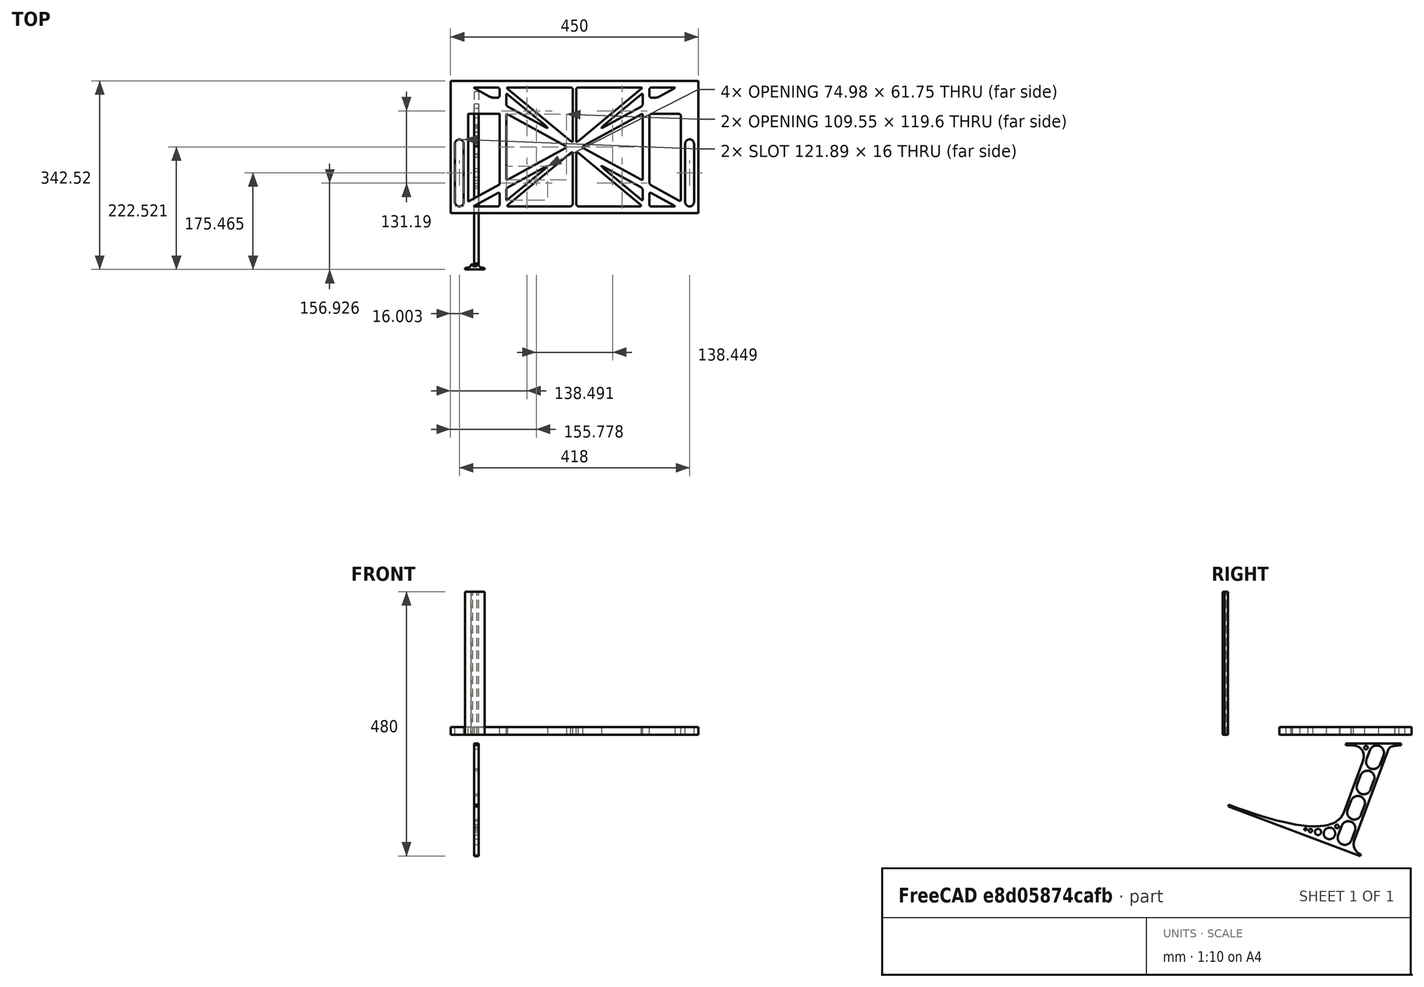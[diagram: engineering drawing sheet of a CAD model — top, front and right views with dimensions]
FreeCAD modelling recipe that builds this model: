
FCSTD DOCUMENT  (FreeCAD 0.19R0.19.2)
Label: laptopStand145FCStd
License: All rights reserved
LicenseURL: http://en.wikipedia.org/wiki/All_rights_reserved
objects: Sketcher::SketchObject×4, Part::Extrusion×3
note: 7 computed .brp shape members not serialized (recipe doc carries the construction recipe); baked Part::Feature solids carry a one-line shape summary decoded from their .brp

FEATURE [Sketcher::SketchObject] Sketch
  FullyConstrained = false
  sketch-geometry (349):
    g0: LineSegment StartX=-10.9272 StartY=-82.7794 StartZ=0 EndX=46.0728 EndY=-51.4823 EndZ=0
    g1: LineSegment StartX=-10.9272 StartY=76.4095 StartZ=0 EndX=-10.9272 EndY=-82.7794 EndZ=0
    g2: LineSegment StartX=46.0728 StartY=76.4095 StartZ=0 EndX=46.0728 EndY=-51.4823 EndZ=0
    g3: LineSegment StartX=-42.9272 StartY=136.221 StartZ=0 EndX=-42.9272 EndY=-103.779 EndZ=0
    g4: LineSegment StartX=407.073 StartY=136.221 StartZ=0 EndX=407.073 EndY=-103.779 EndZ=0
    g5: ArcOfCircle CenterX=-26.9272 CenterY=-83.7794 CenterZ=0 NormalX=0 NormalY=0 NormalZ=1 AngleXU=0 Radius=8 StartAngle=3.14159 EndAngle=6.28319
    g6: ArcOfCircle CenterX=391.073 CenterY=22.1087 CenterZ=0 NormalX=0 NormalY=0 NormalZ=1 AngleXU=0 Radius=8 StartAngle=-4.4e-15 EndAngle=3.14159
    g7: LineSegment StartX=399.073 StartY=22.1087 StartZ=0 EndX=399.073 EndY=-83.7794 EndZ=0
    g8: LineSegment StartX=383.073 StartY=22.1087 StartZ=0 EndX=383.073 EndY=-83.7794 EndZ=0
    g9: ArcOfCircle CenterX=391.073 CenterY=-83.7794 CenterZ=0 NormalX=0 NormalY=0 NormalZ=1 AngleXU=0 Radius=8 StartAngle=3.14159 EndAngle=6.28319
    g10: Circle CenterX=175.022 CenterY=27.0628 CenterZ=0 NormalX=0 NormalY=0 NormalZ=1 AngleXU=0 Radius=1
    g11: Circle CenterX=179.022 CenterY=24.8665 CenterZ=0 NormalX=0 NormalY=0 NormalZ=1 AngleXU=0 Radius=1
    g12: Circle CenterX=179.022 CenterY=27.0628 CenterZ=0 NormalX=0 NormalY=0 NormalZ=1 AngleXU=0 Radius=1
    g13: BSplineCurve PolesCount=3 KnotsCount=2 Degree=2 IsPeriodic=0
    g14: GeomPoint X=175.022 Y=27.0628 Z=0
    g15: GeomPoint X=179.022 Y=27.0628 Z=0
    g16: Circle CenterX=189.124 CenterY=27.0628 CenterZ=0 NormalX=0 NormalY=0 NormalZ=1 AngleXU=0 Radius=1
    g17: Circle CenterX=185.124 CenterY=24.8665 CenterZ=0 NormalX=0 NormalY=0 NormalZ=1 AngleXU=0 Radius=1
    g18: Circle CenterX=185.124 CenterY=27.0628 CenterZ=0 NormalX=0 NormalY=0 NormalZ=1 AngleXU=0 Radius=1
    g19: BSplineCurve PolesCount=3 KnotsCount=2 Degree=2 IsPeriodic=0
    g20: GeomPoint X=189.124 Y=27.0628 Z=0
    g21: GeomPoint X=185.124 Y=27.0628 Z=0
    g22: Circle CenterX=175.022 CenterY=5.37834 CenterZ=0 NormalX=0 NormalY=0 NormalZ=1 AngleXU=0 Radius=1
    g23: Circle CenterX=179.022 CenterY=7.57463 CenterZ=0 NormalX=0 NormalY=0 NormalZ=1 AngleXU=0 Radius=1
    g24: Circle CenterX=179.022 CenterY=5.34704 CenterZ=0 NormalX=0 NormalY=0 NormalZ=1 AngleXU=0 Radius=1
    g25: BSplineCurve PolesCount=3 KnotsCount=2 Degree=2 IsPeriodic=0
    g26: GeomPoint X=175.022 Y=5.37834 Z=0
    g27: GeomPoint X=179.022 Y=5.34704 Z=0
    g28: Circle CenterX=189.124 CenterY=5.37834 CenterZ=0 NormalX=0 NormalY=0 NormalZ=1 AngleXU=0 Radius=1
    g29: Circle CenterX=185.124 CenterY=7.57463 CenterZ=0 NormalX=0 NormalY=0 NormalZ=1 AngleXU=0 Radius=1
    g30: Circle CenterX=185.124 CenterY=5.34704 CenterZ=0 NormalX=0 NormalY=0 NormalZ=1 AngleXU=0 Radius=1
    g31: BSplineCurve PolesCount=3 KnotsCount=2 Degree=2 IsPeriodic=0
    g32: GeomPoint X=189.124 Y=5.37834 Z=0
    g33: GeomPoint X=185.124 Y=5.34704 Z=0
    g34: Circle CenterX=165.871 CenterY=18.1458 CenterZ=0 NormalX=0 NormalY=0 NormalZ=1 AngleXU=0 Radius=1
    g35: Circle CenterX=169.377 CenterY=16.2206 CenterZ=0 NormalX=0 NormalY=0 NormalZ=1 AngleXU=0 Radius=1
    g36: Circle CenterX=165.871 CenterY=14.2954 CenterZ=0 NormalX=0 NormalY=0 NormalZ=1 AngleXU=0 Radius=1
    g37: BSplineCurve PolesCount=3 KnotsCount=2 Degree=2 IsPeriodic=0
    g38: GeomPoint X=165.871 Y=18.1458 Z=0
    g39: GeomPoint X=165.871 Y=14.2954 Z=0
    g40: Circle CenterX=198.275 CenterY=18.1458 CenterZ=0 NormalX=0 NormalY=0 NormalZ=1 AngleXU=0 Radius=1
    g41: Circle CenterX=194.768 CenterY=16.2206 CenterZ=0 NormalX=0 NormalY=0 NormalZ=1 AngleXU=0 Radius=1
    g42: Circle CenterX=198.275 CenterY=14.2954 CenterZ=0 NormalX=0 NormalY=0 NormalZ=1 AngleXU=0 Radius=1
    g43: BSplineCurve PolesCount=3 KnotsCount=2 Degree=2 IsPeriodic=0
    g44: GeomPoint X=198.275 Y=18.1458 Z=0
    g45: GeomPoint X=198.275 Y=14.2954 Z=0
    g46: LineSegment StartX=407.073 StartY=-103.779 StartZ=0 EndX=-42.9272 EndY=-103.779 EndZ=0
    g47: LineSegment StartX=407.073 StartY=136.221 StartZ=0 EndX=-42.9272 EndY=136.221 EndZ=0
    g48: LineSegment StartX=46.0728 StartY=76.4095 StartZ=0 EndX=-10.9272 EndY=76.4095 EndZ=0
    g49: Circle CenterX=125.607 CenterY=54.1951 CenterZ=0 NormalX=0 NormalY=0 NormalZ=1 AngleXU=0 Radius=1
    g50: Circle CenterX=139.632 CenterY=46.4944 CenterZ=0 NormalX=0 NormalY=0 NormalZ=1 AngleXU=0 Radius=1
    g51: Circle CenterX=127.326 CenterY=56.7187 CenterZ=0 NormalX=0 NormalY=0 NormalZ=1 AngleXU=0 Radius=1
    g52: BSplineCurve PolesCount=3 KnotsCount=2 Degree=2 IsPeriodic=0
    g53: GeomPoint X=125.607 Y=54.1951 Z=0
    g54: GeomPoint X=127.326 Y=56.7187 Z=0
    g55: Circle CenterX=236.821 CenterY=56.7187 CenterZ=0 NormalX=0 NormalY=0 NormalZ=1 AngleXU=0 Radius=1
    g56: Circle CenterX=224.513 CenterY=46.4944 CenterZ=0 NormalX=0 NormalY=0 NormalZ=1 AngleXU=0 Radius=1
    g57: Circle CenterX=238.538 CenterY=54.1951 CenterZ=0 NormalX=0 NormalY=0 NormalZ=1 AngleXU=0 Radius=1
    g58: BSplineCurve PolesCount=3 KnotsCount=2 Degree=2 IsPeriodic=0
    g59: GeomPoint X=236.821 Y=56.7187 Z=0
    g60: GeomPoint X=238.538 Y=54.1951 Z=0
    g61: Circle CenterX=238.538 CenterY=-21.7539 CenterZ=0 NormalX=0 NormalY=0 NormalZ=1 AngleXU=0 Radius=1
    g62: Circle CenterX=224.513 CenterY=-14.0532 CenterZ=0 NormalX=0 NormalY=0 NormalZ=1 AngleXU=0 Radius=1
    g63: Circle CenterX=236.821 CenterY=-24.2775 CenterZ=0 NormalX=0 NormalY=0 NormalZ=1 AngleXU=0 Radius=1
    g64: BSplineCurve PolesCount=3 KnotsCount=2 Degree=2 IsPeriodic=0
    g65: GeomPoint X=238.538 Y=-21.7539 Z=0
    g66: GeomPoint X=236.821 Y=-24.2775 Z=0
    g67: Circle CenterX=125.607 CenterY=-21.7539 CenterZ=0 NormalX=0 NormalY=0 NormalZ=1 AngleXU=0 Radius=1
    g68: Circle CenterX=139.632 CenterY=-14.0532 CenterZ=0 NormalX=0 NormalY=0 NormalZ=1 AngleXU=0 Radius=1
    g69: Circle CenterX=127.325 CenterY=-24.2775 CenterZ=0 NormalX=0 NormalY=0 NormalZ=1 AngleXU=0 Radius=1
    g70: BSplineCurve PolesCount=3 KnotsCount=2 Degree=2 IsPeriodic=0
    g71: GeomPoint X=125.607 Y=-21.7539 Z=0
    g72: GeomPoint X=127.325 Y=-24.2775 Z=0
    g73: Circle CenterX=302.996 CenterY=111.695 CenterZ=0 NormalX=0 NormalY=0 NormalZ=1 AngleXU=0 Radius=1
    g74: Circle CenterX=306.073 CenterY=114.251 CenterZ=0 NormalX=0 NormalY=0 NormalZ=1 AngleXU=0 Radius=1
    g75: Circle CenterX=306.073 CenterY=110.251 CenterZ=0 NormalX=0 NormalY=0 NormalZ=1 AngleXU=0 Radius=1
    g76: BSplineCurve PolesCount=3 KnotsCount=2 Degree=2 IsPeriodic=0
    g77: GeomPoint X=302.996 Y=111.695 Z=0
    g78: GeomPoint X=306.073 Y=110.251 Z=0
    g79: Circle CenterX=306.073 CenterY=95.2763 CenterZ=0 NormalX=0 NormalY=0 NormalZ=1 AngleXU=0 Radius=1
    g80: Circle CenterX=306.073 CenterY=91.2763 CenterZ=0 NormalX=0 NormalY=0 NormalZ=1 AngleXU=0 Radius=1
    g81: Circle CenterX=302.567 CenterY=89.3511 CenterZ=0 NormalX=0 NormalY=0 NormalZ=1 AngleXU=0 Radius=1
    g82: BSplineCurve PolesCount=3 KnotsCount=2 Degree=2 IsPeriodic=0
    g83: GeomPoint X=306.073 Y=95.2763 Z=0
    g84: GeomPoint X=302.567 Y=89.3511 Z=0
    g85: LineSegment StartX=306.073 StartY=110.251 StartZ=0 EndX=306.073 EndY=95.2763 EndZ=0
    g86: LineSegment StartX=302.996 StartY=111.695 StartZ=0 EndX=236.821 EndY=56.7187 EndZ=0
    g87: LineSegment StartX=238.538 StartY=54.1951 StartZ=0 EndX=302.567 EndY=89.3511 EndZ=0
    g88: Circle CenterX=61.1496 CenterY=111.695 CenterZ=0 NormalX=0 NormalY=0 NormalZ=1 AngleXU=0 Radius=1
    g89: Circle CenterX=58.0728 CenterY=114.251 CenterZ=0 NormalX=0 NormalY=0 NormalZ=1 AngleXU=0 Radius=1
    g90: Circle CenterX=58.0728 CenterY=110.251 CenterZ=0 NormalX=0 NormalY=0 NormalZ=1 AngleXU=0 Radius=1
    g91: BSplineCurve PolesCount=3 KnotsCount=2 Degree=2 IsPeriodic=0
    g92: GeomPoint X=61.1496 Y=111.695 Z=0
    g93: GeomPoint X=58.0728 Y=110.251 Z=0
    g94: Circle CenterX=61.5791 CenterY=89.3511 CenterZ=0 NormalX=0 NormalY=0 NormalZ=1 AngleXU=0 Radius=1
    g95: Circle CenterX=58.0728 CenterY=91.2763 CenterZ=0 NormalX=0 NormalY=0 NormalZ=1 AngleXU=0 Radius=1
    g96: Circle CenterX=58.0728 CenterY=95.2763 CenterZ=0 NormalX=0 NormalY=0 NormalZ=1 AngleXU=0 Radius=1
    g97: BSplineCurve PolesCount=3 KnotsCount=2 Degree=2 IsPeriodic=0
    g98: GeomPoint X=61.5791 Y=89.3511 Z=0
    g99: GeomPoint X=58.0728 Y=95.2763 Z=0
    g100: LineSegment StartX=58.0728 StartY=110.251 StartZ=0 EndX=58.0728 EndY=95.2763 EndZ=0
    g101: LineSegment StartX=61.1496 StartY=111.695 StartZ=0 EndX=127.326 EndY=56.7187 EndZ=0
    g102: LineSegment StartX=125.607 StartY=54.1951 StartZ=0 EndX=61.5791 EndY=89.3511 EndZ=0
    g103: Circle CenterX=61.5791 CenterY=-56.9099 CenterZ=0 NormalX=0 NormalY=0 NormalZ=1 AngleXU=0 Radius=1
    g104: Circle CenterX=58.0728 CenterY=-58.8351 CenterZ=0 NormalX=0 NormalY=0 NormalZ=1 AngleXU=0 Radius=1
    g105: Circle CenterX=58.0728 CenterY=-62.8351 CenterZ=0 NormalX=0 NormalY=0 NormalZ=1 AngleXU=0 Radius=1
    g106: BSplineCurve PolesCount=3 KnotsCount=2 Degree=2 IsPeriodic=0
    g107: GeomPoint X=61.5791 Y=-56.9099 Z=0
    g108: GeomPoint X=58.0728 Y=-62.8351 Z=0
    g109: Circle CenterX=58.0728 CenterY=-77.8102 CenterZ=0 NormalX=0 NormalY=0 NormalZ=1 AngleXU=0 Radius=1
    g110: Circle CenterX=58.0728 CenterY=-81.8102 CenterZ=0 NormalX=0 NormalY=0 NormalZ=1 AngleXU=0 Radius=1
    g111: Circle CenterX=61.1496 CenterY=-79.2541 CenterZ=0 NormalX=0 NormalY=0 NormalZ=1 AngleXU=0 Radius=1
    g112: BSplineCurve PolesCount=3 KnotsCount=2 Degree=2 IsPeriodic=0
    g113: GeomPoint X=58.0728 Y=-77.8102 Z=0
    g114: GeomPoint X=61.1496 Y=-79.2541 Z=0
    g115: LineSegment StartX=58.0728 StartY=-62.8351 StartZ=0 EndX=58.0728 EndY=-77.8102 EndZ=0
    g116: LineSegment StartX=61.1496 StartY=-79.2541 StartZ=0 EndX=127.325 EndY=-24.2775 EndZ=0
    g117: LineSegment StartX=125.607 StartY=-21.7539 StartZ=0 EndX=61.5791 EndY=-56.9099 EndZ=0
    g118: Circle CenterX=302.567 CenterY=-56.9099 CenterZ=0 NormalX=0 NormalY=0 NormalZ=1 AngleXU=0 Radius=1
    g119: Circle CenterX=306.073 CenterY=-58.8351 CenterZ=0 NormalX=0 NormalY=0 NormalZ=1 AngleXU=0 Radius=1
    g120: Circle CenterX=306.073 CenterY=-62.8351 CenterZ=0 NormalX=0 NormalY=0 NormalZ=1 AngleXU=0 Radius=1
    g121: BSplineCurve PolesCount=3 KnotsCount=2 Degree=2 IsPeriodic=0
    g122: GeomPoint X=302.567 Y=-56.9099 Z=0
    g123: GeomPoint X=306.073 Y=-62.8351 Z=0
    g124: Circle CenterX=302.996 CenterY=-79.2541 CenterZ=0 NormalX=0 NormalY=0 NormalZ=1 AngleXU=0 Radius=1
    g125: Circle CenterX=306.073 CenterY=-81.8102 CenterZ=0 NormalX=0 NormalY=0 NormalZ=1 AngleXU=0 Radius=1
    g126: Circle CenterX=306.073 CenterY=-77.8102 CenterZ=0 NormalX=0 NormalY=0 NormalZ=1 AngleXU=0 Radius=1
    g127: BSplineCurve PolesCount=3 KnotsCount=2 Degree=2 IsPeriodic=0
    g128: GeomPoint X=302.996 Y=-79.2541 Z=0
    g129: GeomPoint X=306.073 Y=-77.8102 Z=0
    g130: LineSegment StartX=306.073 StartY=-62.8351 StartZ=0 EndX=306.073 EndY=-77.8102 EndZ=0
    g131: LineSegment StartX=302.996 StartY=-79.2541 StartZ=0 EndX=236.821 EndY=-24.2775 EndZ=0
    g132: LineSegment StartX=238.538 StartY=-21.7539 StartZ=0 EndX=302.567 EndY=-56.9099 EndZ=0
    g133: Circle CenterX=61.6457 CenterY=-88.8112 CenterZ=0 NormalX=0 NormalY=0 NormalZ=1 AngleXU=0 Radius=1
    g134: Circle CenterX=58.0728 CenterY=-91.7794 CenterZ=0 NormalX=0 NormalY=0 NormalZ=1 AngleXU=0 Radius=1
    g135: Circle CenterX=63.9135 CenterY=-91.7794 CenterZ=0 NormalX=0 NormalY=0 NormalZ=1 AngleXU=0 Radius=1
    g136: BSplineCurve PolesCount=3 KnotsCount=2 Degree=2 IsPeriodic=0
    g137: GeomPoint X=61.6457 Y=-88.8112 Z=0
    g138: GeomPoint X=63.9135 Y=-91.7794 Z=0
    g139: Circle CenterX=179.022 CenterY=-85.8163 CenterZ=0 NormalX=0 NormalY=0 NormalZ=1 AngleXU=0 Radius=1
    g140: Circle CenterX=179.022 CenterY=-91.7794 CenterZ=0 NormalX=0 NormalY=0 NormalZ=1 AngleXU=0 Radius=1
    g141: Circle CenterX=171.895 CenterY=-91.7794 CenterZ=0 NormalX=0 NormalY=0 NormalZ=1 AngleXU=0 Radius=1
    g142: BSplineCurve PolesCount=3 KnotsCount=2 Degree=2 IsPeriodic=0
    g143: GeomPoint X=179.022 Y=-85.8163 Z=0
    g144: GeomPoint X=171.895 Y=-91.7794 Z=0
    g145: Circle CenterX=185.124 CenterY=-86.2028 CenterZ=0 NormalX=0 NormalY=0 NormalZ=1 AngleXU=0 Radius=1
    g146: Circle CenterX=185.124 CenterY=-91.7794 CenterZ=0 NormalX=0 NormalY=0 NormalZ=1 AngleXU=0 Radius=1
    g147: Circle CenterX=191.747 CenterY=-91.7794 CenterZ=0 NormalX=0 NormalY=0 NormalZ=1 AngleXU=0 Radius=1
    g148: BSplineCurve PolesCount=3 KnotsCount=2 Degree=2 IsPeriodic=0
    g149: GeomPoint X=185.124 Y=-86.2028 Z=0
    g150: GeomPoint X=191.747 Y=-91.7794 Z=0
    g151: Circle CenterX=299.888 CenterY=-86.6413 CenterZ=0 NormalX=0 NormalY=0 NormalZ=1 AngleXU=0 Radius=1
    g152: Circle CenterX=306.073 CenterY=-91.7794 CenterZ=0 NormalX=0 NormalY=0 NormalZ=1 AngleXU=0 Radius=1
    g153: Circle CenterX=298.776 CenterY=-91.7794 CenterZ=0 NormalX=0 NormalY=0 NormalZ=1 AngleXU=0 Radius=1
    g154: BSplineCurve PolesCount=3 KnotsCount=2 Degree=2 IsPeriodic=0
    g155: GeomPoint X=299.888 Y=-86.6413 Z=0
    g156: GeomPoint X=298.776 Y=-91.7794 Z=0
    g157: LineSegment StartX=189.124 StartY=5.37834 StartZ=0 EndX=299.888 EndY=-86.6413 EndZ=0
    g158: LineSegment StartX=298.776 StartY=-91.7794 StartZ=0 EndX=191.747 EndY=-91.7794 EndZ=0
    g159: LineSegment StartX=185.124 StartY=-86.2028 StartZ=0 EndX=185.124 EndY=5.34704 EndZ=0
    g160: LineSegment StartX=179.022 StartY=5.34704 StartZ=0 EndX=179.022 EndY=-85.8163 EndZ=0
    g161: LineSegment StartX=171.895 StartY=-91.7794 StartZ=0 EndX=63.9135 EndY=-91.7794 EndZ=0
    g162: LineSegment StartX=61.6457 StartY=-88.8112 StartZ=0 EndX=175.022 EndY=5.37834 EndZ=0
    g163: Circle CenterX=302.073 CenterY=124.221 CenterZ=0 NormalX=0 NormalY=0 NormalZ=1 AngleXU=0 Radius=1
    g164: Circle CenterX=306.073 CenterY=124.221 CenterZ=0 NormalX=0 NormalY=0 NormalZ=1 AngleXU=0 Radius=1
    g165: Circle CenterX=302.996 CenterY=121.665 CenterZ=0 NormalX=0 NormalY=0 NormalZ=1 AngleXU=0 Radius=1
    g166: BSplineCurve PolesCount=3 KnotsCount=2 Degree=2 IsPeriodic=0
    g167: GeomPoint X=302.073 Y=124.221 Z=0
    g168: GeomPoint X=302.996 Y=121.665 Z=0
    g169: Circle CenterX=189.124 CenterY=124.221 CenterZ=0 NormalX=0 NormalY=0 NormalZ=1 AngleXU=0 Radius=1
    g170: Circle CenterX=185.124 CenterY=124.221 CenterZ=0 NormalX=0 NormalY=0 NormalZ=1 AngleXU=0 Radius=1
    g171: Circle CenterX=185.124 CenterY=120.221 CenterZ=0 NormalX=0 NormalY=0 NormalZ=1 AngleXU=0 Radius=1
    g172: BSplineCurve PolesCount=3 KnotsCount=2 Degree=2 IsPeriodic=0
    g173: GeomPoint X=189.124 Y=124.221 Z=0
    g174: GeomPoint X=185.124 Y=120.221 Z=0
    g175: Circle CenterX=175.022 CenterY=124.221 CenterZ=0 NormalX=0 NormalY=0 NormalZ=1 AngleXU=0 Radius=1
    g176: Circle CenterX=179.022 CenterY=124.221 CenterZ=0 NormalX=0 NormalY=0 NormalZ=1 AngleXU=0 Radius=1
    g177: Circle CenterX=179.022 CenterY=120.221 CenterZ=0 NormalX=0 NormalY=0 NormalZ=1 AngleXU=0 Radius=1
    g178: BSplineCurve PolesCount=3 KnotsCount=2 Degree=2 IsPeriodic=0
    g179: GeomPoint X=175.022 Y=124.221 Z=0
    g180: GeomPoint X=179.022 Y=120.221 Z=0
    g181: Circle CenterX=62.0728 CenterY=124.221 CenterZ=0 NormalX=0 NormalY=0 NormalZ=1 AngleXU=0 Radius=1
    g182: Circle CenterX=58.0728 CenterY=124.221 CenterZ=0 NormalX=0 NormalY=0 NormalZ=1 AngleXU=0 Radius=1
    g183: Circle CenterX=61.1496 CenterY=121.665 CenterZ=0 NormalX=0 NormalY=0 NormalZ=1 AngleXU=0 Radius=1
    g184: BSplineCurve PolesCount=3 KnotsCount=2 Degree=2 IsPeriodic=0
    g185: GeomPoint X=62.0728 Y=124.221 Z=0
    g186: GeomPoint X=61.1496 Y=121.665 Z=0
    g187: LineSegment StartX=62.0728 StartY=124.221 StartZ=0 EndX=175.022 EndY=124.221 EndZ=0
    g188: LineSegment StartX=179.022 StartY=120.221 StartZ=0 EndX=179.022 EndY=27.0628 EndZ=0
    g189: LineSegment StartX=185.124 StartY=27.0628 StartZ=0 EndX=185.124 EndY=120.221 EndZ=0
    g190: LineSegment StartX=189.124 StartY=124.221 StartZ=0 EndX=302.073 EndY=124.221 EndZ=0
    g191: LineSegment StartX=302.996 StartY=121.665 StartZ=0 EndX=189.124 EndY=27.0628 EndZ=0
    g192: LineSegment StartX=175.022 StartY=27.0628 StartZ=0 EndX=61.1496 EndY=121.665 EndZ=0
    g193: Circle CenterX=61.5791 CenterY=75.4095 CenterZ=0 NormalX=0 NormalY=0 NormalZ=1 AngleXU=0 Radius=1
    g194: Circle CenterX=58.0728 CenterY=77.3346 CenterZ=0 NormalX=0 NormalY=0 NormalZ=1 AngleXU=0 Radius=1
    g195: Circle CenterX=58.0728 CenterY=73.3346 CenterZ=0 NormalX=0 NormalY=0 NormalZ=1 AngleXU=0 Radius=1
    g196: BSplineCurve PolesCount=3 KnotsCount=2 Degree=2 IsPeriodic=0
    g197: GeomPoint X=61.5791 Y=75.4095 Z=0
    g198: GeomPoint X=58.0728 Y=73.3346 Z=0
    g199: Circle CenterX=58.0728 CenterY=-40.8935 CenterZ=0 NormalX=0 NormalY=0 NormalZ=1 AngleXU=0 Radius=1
    g200: Circle CenterX=58.0728 CenterY=-44.8935 CenterZ=0 NormalX=0 NormalY=0 NormalZ=1 AngleXU=0 Radius=1
    g201: Circle CenterX=61.5791 CenterY=-42.9683 CenterZ=0 NormalX=0 NormalY=0 NormalZ=1 AngleXU=0 Radius=1
    g202: BSplineCurve PolesCount=3 KnotsCount=2 Degree=2 IsPeriodic=0
    g203: GeomPoint X=58.0728 Y=-40.8935 Z=0
    g204: GeomPoint X=61.5791 Y=-42.9683 Z=0
    g205: LineSegment StartX=61.5791 StartY=-42.9683 StartZ=0 EndX=165.871 EndY=14.2954 EndZ=0
    g206: LineSegment StartX=165.871 StartY=18.1458 StartZ=0 EndX=61.5791 EndY=75.4095 EndZ=0
    g207: LineSegment StartX=58.0728 StartY=73.3346 StartZ=0 EndX=58.0728 EndY=-40.8935 EndZ=0
    g208: Circle CenterX=302.567 CenterY=-42.9683 CenterZ=0 NormalX=0 NormalY=0 NormalZ=1 AngleXU=0 Radius=1
    g209: Circle CenterX=306.073 CenterY=-44.8935 CenterZ=0 NormalX=0 NormalY=0 NormalZ=1 AngleXU=0 Radius=1
    g210: Circle CenterX=306.073 CenterY=-40.8935 CenterZ=0 NormalX=0 NormalY=0 NormalZ=1 AngleXU=0 Radius=1
    g211: BSplineCurve PolesCount=3 KnotsCount=2 Degree=2 IsPeriodic=0
    g212: GeomPoint X=302.567 Y=-42.9683 Z=0
    g213: GeomPoint X=306.073 Y=-40.8935 Z=0
    g214: Circle CenterX=306.073 CenterY=73.3346 CenterZ=0 NormalX=0 NormalY=0 NormalZ=1 AngleXU=0 Radius=1
    g215: Circle CenterX=306.073 CenterY=77.3346 CenterZ=0 NormalX=0 NormalY=0 NormalZ=1 AngleXU=0 Radius=1
    g216: Circle CenterX=302.567 CenterY=75.4095 CenterZ=0 NormalX=0 NormalY=0 NormalZ=1 AngleXU=0 Radius=1
    g217: BSplineCurve PolesCount=3 KnotsCount=2 Degree=2 IsPeriodic=0
    g218: GeomPoint X=306.073 Y=73.3346 Z=0
    g219: GeomPoint X=302.567 Y=75.4095 Z=0
    g220: LineSegment StartX=302.567 StartY=-42.9683 StartZ=0 EndX=198.275 EndY=14.2954 EndZ=0
    g221: LineSegment StartX=198.275 StartY=18.1458 StartZ=0 EndX=302.567 EndY=75.4095 EndZ=0
    g222: LineSegment StartX=306.073 StartY=73.3346 StartZ=0 EndX=306.073 EndY=-40.8935 EndZ=0
    g223: LineSegment StartX=322.073 StartY=105.865 StartZ=0 EndX=328.643 EndY=105.865 EndZ=0
    g224: LineSegment StartX=318.073 StartY=120.221 StartZ=0 EndX=318.073 EndY=109.865 EndZ=0
    g225: LineSegment StartX=336.157 StartY=107.779 StartZ=0 EndX=362.567 EndY=122.294 EndZ=0
    g226: Circle CenterX=362.073 CenterY=124.221 CenterZ=0 NormalX=0 NormalY=0 NormalZ=1 AngleXU=0 Radius=1
    g227: Circle CenterX=366.073 CenterY=124.221 CenterZ=0 NormalX=0 NormalY=0 NormalZ=1 AngleXU=0 Radius=1
    g228: Circle CenterX=362.567 CenterY=122.294 CenterZ=0 NormalX=0 NormalY=0 NormalZ=1 AngleXU=0 Radius=1
    g229: BSplineCurve PolesCount=3 KnotsCount=2 Degree=2 IsPeriodic=0
    g230: GeomPoint X=362.073 Y=124.221 Z=0
    g231: GeomPoint X=362.567 Y=122.294 Z=0
    g232: Circle CenterX=322.073 CenterY=124.221 CenterZ=0 NormalX=0 NormalY=0 NormalZ=1 AngleXU=0 Radius=1
    g233: Circle CenterX=318.073 CenterY=124.221 CenterZ=0 NormalX=0 NormalY=0 NormalZ=1 AngleXU=0 Radius=1
    g234: Circle CenterX=318.073 CenterY=120.221 CenterZ=0 NormalX=0 NormalY=0 NormalZ=1 AngleXU=0 Radius=1
    g235: BSplineCurve PolesCount=3 KnotsCount=2 Degree=2 IsPeriodic=0
    g236: GeomPoint X=322.073 Y=124.221 Z=0
    g237: GeomPoint X=318.073 Y=120.221 Z=0
    g238: Circle CenterX=322.073 CenterY=105.865 CenterZ=0 NormalX=0 NormalY=0 NormalZ=1 AngleXU=0 Radius=1
    g239: Circle CenterX=318.073 CenterY=105.865 CenterZ=0 NormalX=0 NormalY=0 NormalZ=1 AngleXU=0 Radius=1
    g240: Circle CenterX=318.073 CenterY=109.865 CenterZ=0 NormalX=0 NormalY=0 NormalZ=1 AngleXU=0 Radius=1
    g241: BSplineCurve PolesCount=3 KnotsCount=2 Degree=2 IsPeriodic=0
    g242: GeomPoint X=322.073 Y=105.865 Z=0
    g243: GeomPoint X=318.073 Y=109.865 Z=0
    g244: Circle CenterX=336.157 CenterY=107.779 CenterZ=0 NormalX=0 NormalY=0 NormalZ=1 AngleXU=0 Radius=1
    g245: Circle CenterX=332.651 CenterY=105.853 CenterZ=0 NormalX=0 NormalY=0 NormalZ=1 AngleXU=0 Radius=1
    g246: Circle CenterX=328.643 CenterY=105.865 CenterZ=0 NormalX=0 NormalY=0 NormalZ=1 AngleXU=0 Radius=1
    g247: BSplineCurve PolesCount=3 KnotsCount=2 Degree=2 IsPeriodic=0
    g248: GeomPoint X=336.157 Y=107.779 Z=0
    g249: GeomPoint X=328.643 Y=105.865 Z=0
    g250: LineSegment StartX=322.073 StartY=124.221 StartZ=0 EndX=362.073 EndY=124.221 EndZ=0
    g251: Circle CenterX=371.567 CenterY=-80.8644 CenterZ=0 NormalX=0 NormalY=0 NormalZ=1 AngleXU=0 Radius=1
    g252: Circle CenterX=375.073 CenterY=-82.7896 CenterZ=0 NormalX=0 NormalY=0 NormalZ=1 AngleXU=0 Radius=1
    g253: Circle CenterX=375.073 CenterY=-78.7896 CenterZ=0 NormalX=0 NormalY=0 NormalZ=1 AngleXU=0 Radius=1
    g254: BSplineCurve PolesCount=3 KnotsCount=2 Degree=2 IsPeriodic=0
    g255: GeomPoint X=371.567 Y=-80.8644 Z=0
    g256: GeomPoint X=375.073 Y=-78.7896 Z=0
    g257: Circle CenterX=321.579 CenterY=-53.4075 CenterZ=0 NormalX=0 NormalY=0 NormalZ=1 AngleXU=0 Radius=1
    g258: Circle CenterX=318.073 CenterY=-51.4823 CenterZ=0 NormalX=0 NormalY=0 NormalZ=1 AngleXU=0 Radius=1
    g259: Circle CenterX=318.073 CenterY=-47.4805 CenterZ=0 NormalX=0 NormalY=0 NormalZ=1 AngleXU=0 Radius=1
    g260: BSplineCurve PolesCount=3 KnotsCount=2 Degree=2 IsPeriodic=0
    g261: GeomPoint X=321.579 Y=-53.4075 Z=0
    g262: GeomPoint X=318.073 Y=-47.4805 Z=0
    g263: LineSegment StartX=371.567 StartY=-80.8644 StartZ=0 EndX=321.579 EndY=-53.4075 EndZ=0
    g264: Circle CenterX=321.579 CenterY=-67.3492 CenterZ=0 NormalX=0 NormalY=0 NormalZ=1 AngleXU=0 Radius=1
    g265: Circle CenterX=318.073 CenterY=-65.424 CenterZ=0 NormalX=0 NormalY=0 NormalZ=1 AngleXU=0 Radius=1
    g266: Circle CenterX=318.073 CenterY=-69.424 CenterZ=0 NormalX=0 NormalY=0 NormalZ=1 AngleXU=0 Radius=1
    g267: BSplineCurve PolesCount=3 KnotsCount=2 Degree=2 IsPeriodic=0
    g268: GeomPoint X=321.579 Y=-67.3492 Z=0
    g269: GeomPoint X=318.073 Y=-69.424 Z=0
    g270: Circle CenterX=362.567 CenterY=-89.8542 CenterZ=0 NormalX=0 NormalY=0 NormalZ=1 AngleXU=0 Radius=1
    g271: Circle CenterX=366.073 CenterY=-91.7794 CenterZ=0 NormalX=0 NormalY=0 NormalZ=1 AngleXU=0 Radius=1
    g272: Circle CenterX=362.073 CenterY=-91.7794 CenterZ=0 NormalX=0 NormalY=0 NormalZ=1 AngleXU=0 Radius=1
    g273: BSplineCurve PolesCount=3 KnotsCount=2 Degree=2 IsPeriodic=0
    g274: GeomPoint X=362.567 Y=-89.8542 Z=0
    g275: GeomPoint X=362.073 Y=-91.7794 Z=0
    g276: Circle CenterX=322.073 CenterY=-91.7794 CenterZ=0 NormalX=0 NormalY=0 NormalZ=1 AngleXU=0 Radius=1
    g277: Circle CenterX=318.073 CenterY=-91.7794 CenterZ=0 NormalX=0 NormalY=0 NormalZ=1 AngleXU=0 Radius=1
    g278: Circle CenterX=318.073 CenterY=-87.7794 CenterZ=0 NormalX=0 NormalY=0 NormalZ=1 AngleXU=0 Radius=1
    g279: BSplineCurve PolesCount=3 KnotsCount=2 Degree=2 IsPeriodic=0
    g280: GeomPoint X=322.073 Y=-91.7794 Z=0
    g281: GeomPoint X=318.073 Y=-87.7794 Z=0
    g282: LineSegment StartX=362.567 StartY=-89.8542 StartZ=0 EndX=321.579 EndY=-67.3492 EndZ=0
    g283: LineSegment StartX=318.073 StartY=-69.424 StartZ=0 EndX=318.073 EndY=-87.7794 EndZ=0
    g284: LineSegment StartX=322.073 StartY=-91.7794 StartZ=0 EndX=362.073 EndY=-91.7794 EndZ=0
    g285: Circle CenterX=2.07281 CenterY=124.221 CenterZ=0 NormalX=0 NormalY=0 NormalZ=1 AngleXU=0 Radius=1
    g286: Circle CenterX=1.57905 CenterY=122.295 CenterZ=0 NormalX=0 NormalY=0 NormalZ=1 AngleXU=0 Radius=1
    g287: BSplineCurve PolesCount=3 KnotsCount=2 Degree=2 IsPeriodic=0
    g288: GeomPoint X=2.07281 Y=124.221 Z=0
    g289: GeomPoint X=1.57905 Y=122.295 Z=0
    g290: Circle CenterX=42.0728 CenterY=124.221 CenterZ=0 NormalX=0 NormalY=0 NormalZ=1 AngleXU=0 Radius=1
    g291: Circle CenterX=46.0728 CenterY=124.221 CenterZ=0 NormalX=0 NormalY=0 NormalZ=1 AngleXU=0 Radius=1
    g292: Circle CenterX=46.0728 CenterY=120.221 CenterZ=0 NormalX=0 NormalY=0 NormalZ=1 AngleXU=0 Radius=1
    g293: BSplineCurve PolesCount=3 KnotsCount=2 Degree=2 IsPeriodic=0
    g294: GeomPoint X=42.0728 Y=124.221 Z=0
    g295: GeomPoint X=46.0728 Y=120.221 Z=0
    g296: Circle CenterX=46.0728 CenterY=109.865 CenterZ=0 NormalX=0 NormalY=0 NormalZ=1 AngleXU=0 Radius=1
    g297: Circle CenterX=46.0728 CenterY=105.865 CenterZ=0 NormalX=0 NormalY=0 NormalZ=1 AngleXU=0 Radius=1
    g298: Circle CenterX=42.0728 CenterY=105.865 CenterZ=0 NormalX=0 NormalY=0 NormalZ=1 AngleXU=0 Radius=1
    g299: BSplineCurve PolesCount=3 KnotsCount=2 Degree=2 IsPeriodic=0
    g300: GeomPoint X=46.0728 Y=109.865 Z=0
    g301: GeomPoint X=42.0728 Y=105.865 Z=0
    g302: Circle CenterX=35.5028 CenterY=105.865 CenterZ=0 NormalX=0 NormalY=0 NormalZ=1 AngleXU=0 Radius=1
    g303: Circle CenterX=31.5028 CenterY=105.865 CenterZ=0 NormalX=0 NormalY=0 NormalZ=1 AngleXU=0 Radius=1
    g304: Circle CenterX=27.9965 CenterY=107.79 CenterZ=0 NormalX=0 NormalY=0 NormalZ=1 AngleXU=0 Radius=1
    g305: BSplineCurve PolesCount=3 KnotsCount=2 Degree=2 IsPeriodic=0
    g306: GeomPoint X=35.5028 Y=105.865 Z=0
    g307: GeomPoint X=27.9965 Y=107.79 Z=0
    g308: LineSegment StartX=2.07281 StartY=124.221 StartZ=0 EndX=42.0728 EndY=124.221 EndZ=0
    g309: LineSegment StartX=46.0728 StartY=120.221 StartZ=0 EndX=46.0728 EndY=109.865 EndZ=0
    g310: LineSegment StartX=42.0728 StartY=105.865 StartZ=0 EndX=35.5028 EndY=105.865 EndZ=0
    g311: LineSegment StartX=27.9965 StartY=107.79 StartZ=0 EndX=1.57905 EndY=122.295 EndZ=0
    g312: Circle CenterX=42.5666 CenterY=-67.3492 CenterZ=0 NormalX=0 NormalY=0 NormalZ=1 AngleXU=0 Radius=1
    g313: Circle CenterX=46.0728 CenterY=-65.424 CenterZ=0 NormalX=0 NormalY=0 NormalZ=1 AngleXU=0 Radius=1
    g314: Circle CenterX=46.0728 CenterY=-69.424 CenterZ=0 NormalX=0 NormalY=0 NormalZ=1 AngleXU=0 Radius=1
    g315: BSplineCurve PolesCount=3 KnotsCount=2 Degree=2 IsPeriodic=0
    g316: GeomPoint X=42.5666 Y=-67.3492 Z=0
    g317: GeomPoint X=46.0728 Y=-69.424 Z=0
    g318: Circle CenterX=46.0728 CenterY=-87.7794 CenterZ=0 NormalX=0 NormalY=0 NormalZ=1 AngleXU=0 Radius=1
    g319: Circle CenterX=46.0728 CenterY=-91.7794 CenterZ=0 NormalX=0 NormalY=0 NormalZ=1 AngleXU=0 Radius=1
    g320: Circle CenterX=42.0728 CenterY=-91.7794 CenterZ=0 NormalX=0 NormalY=0 NormalZ=1 AngleXU=0 Radius=1
    g321: BSplineCurve PolesCount=3 KnotsCount=2 Degree=2 IsPeriodic=0
    g322: GeomPoint X=46.0728 Y=-87.7794 Z=0
    g323: GeomPoint X=42.0728 Y=-91.7794 Z=0
    g324: Circle CenterX=2.07281 CenterY=-91.7794 CenterZ=0 NormalX=0 NormalY=0 NormalZ=1 AngleXU=0 Radius=1
    g325: Circle CenterX=-1.92719 CenterY=-91.7794 CenterZ=0 NormalX=0 NormalY=0 NormalZ=1 AngleXU=0 Radius=1
    g326: Circle CenterX=1.57905 CenterY=-89.8542 CenterZ=0 NormalX=0 NormalY=0 NormalZ=1 AngleXU=0 Radius=1
    g327: BSplineCurve PolesCount=3 KnotsCount=2 Degree=2 IsPeriodic=0
    g328: GeomPoint X=2.07281 Y=-91.7794 Z=0
    g329: GeomPoint X=1.57905 Y=-89.8542 Z=0
    g330: LineSegment StartX=2.07281 StartY=-91.7794 StartZ=0 EndX=42.0728 EndY=-91.7794 EndZ=0
    g331: LineSegment StartX=46.0728 StartY=-87.7794 StartZ=0 EndX=46.0728 EndY=-69.424 EndZ=0
    g332: LineSegment StartX=42.5666 StartY=-67.3492 StartZ=0 EndX=1.57905 EndY=-89.8542 EndZ=0
    g333: Circle CenterX=322.073 CenterY=76.4095 CenterZ=0 NormalX=0 NormalY=0 NormalZ=1 AngleXU=0 Radius=4
    g334: BSplineCurve PolesCount=3 KnotsCount=2 Degree=2 IsPeriodic=0
    g335: GeomPoint X=318.073 Y=72.4095 Z=0
    g336: GeomPoint X=322.073 Y=76.4095 Z=0
    g337: Circle CenterX=375.073 CenterY=72.4095 CenterZ=0 NormalX=0 NormalY=0 NormalZ=1 AngleXU=0 Radius=1
    g338: Circle CenterX=375.073 CenterY=76.4095 CenterZ=0 NormalX=0 NormalY=0 NormalZ=1 AngleXU=0 Radius=1
    g339: Circle CenterX=371.073 CenterY=76.4095 CenterZ=0 NormalX=0 NormalY=0 NormalZ=1 AngleXU=0 Radius=1
    g340: BSplineCurve PolesCount=3 KnotsCount=2 Degree=2 IsPeriodic=0
    g341: GeomPoint X=375.073 Y=72.4095 Z=0
    g342: GeomPoint X=371.073 Y=76.4095 Z=0
    g343: LineSegment StartX=322.073 StartY=76.4095 StartZ=0 EndX=371.073 EndY=76.4095 EndZ=0
    g344: LineSegment StartX=318.073 StartY=72.4095 StartZ=0 EndX=318.073 EndY=-47.4805 EndZ=0
    g345: LineSegment StartX=375.073 StartY=72.4095 StartZ=0 EndX=375.073 EndY=-78.7896 EndZ=0
    g346: ArcOfCircle CenterX=-26.9272 CenterY=22.1087 CenterZ=0 NormalX=0 NormalY=0 NormalZ=1 AngleXU=0 Radius=4 StartAngle=5e-16 EndAngle=3.14159
    g347: LineSegment StartX=-30.9272 StartY=22.1087 StartZ=0 EndX=-34.9272 EndY=-83.7794 EndZ=0
    g348: LineSegment StartX=-18.9272 StartY=-83.7794 StartZ=0 EndX=-22.9272 EndY=22.1087 EndZ=0
  constraints (572):
    c: Coincident(g0,g2)
    c: Block(g0)
    c: Block(g1)
    c: Vertical(g3)
    c: Vertical(g4)
    c: Block(g4)
    c: Block(g3)
    c: Tangent(g6,g7) = 1.5708
    c: Tangent(g7,g9) = 1.5708
    c: Equal(g6,g9)
    c: Coincident(g8,g6)
    c: Coincident(g8,g9)
    c: Block(g7)
    c: Block(g8)
    c: Weight(g10) = 1
    c: Equal(g10,g11)
    c: Equal(g10,g12)
    c: InternalAlignment(g10,g13)
    c: InternalAlignment(g11,g13)
    c: InternalAlignment(g12,g13)
    c: InternalAlignment(g14,g13)
    c: InternalAlignment(g15,g13)
    c: Weight(g16) = 1
    c: Equal(g16,g17)
    c: Equal(g16,g18)
    c: InternalAlignment(g16,g19)
    c: InternalAlignment(g17,g19)
    c: InternalAlignment(g18,g19)
    c: InternalAlignment(g20,g19)
    c: InternalAlignment(g21,g19)
    c: Block(g19)
    c: Block(g13)
    c: Weight(g22) = 1
    c: Equal(g22,g23)
    c: Equal(g22,g24)
    c: InternalAlignment(g22,g25)
    c: InternalAlignment(g23,g25)
    c: InternalAlignment(g24,g25)
    c: InternalAlignment(g26,g25)
    c: InternalAlignment(g27,g25)
    c: Weight(g28) = 1
    c: Equal(g28,g29)
    c: Equal(g28,g30)
    c: InternalAlignment(g28,g31)
    c: InternalAlignment(g29,g31)
    c: InternalAlignment(g30,g31)
    c: InternalAlignment(g32,g31)
    c: InternalAlignment(g33,g31)
    c: Block(g31)
    c: Block(g25)
    c: Weight(g34) = 1
    c: Equal(g34,g35)
    c: Equal(g34,g36)
    c: InternalAlignment(g34,g37)
    c: InternalAlignment(g35,g37)
    c: InternalAlignment(g36,g37)
    c: InternalAlignment(g38,g37)
    c: InternalAlignment(g39,g37)
    c: Weight(g40) = 1
    c: Equal(g40,g41)
    c: Equal(g40,g42)
    c: InternalAlignment(g40,g43)
    c: InternalAlignment(g41,g43)
    c: InternalAlignment(g42,g43)
    c: InternalAlignment(g44,g43)
    c: InternalAlignment(g45,g43)
    c: Block(g37)
    c: Block(g43)
    c: Coincident(g46,g4)
    c: Coincident(g46,g3)
    c: Horizontal(g46)
    c: Distance(g46) = 450
    c: Coincident(g47,g4)
    c: Coincident(g47,g3)
    c: Horizontal(g47)
    c: Horizontal(g48)
    c: Coincident(g2,g48)
    c: Block(g48)
    c: Coincident(g1,g48)
    c: Weight(g49) = 1
    c: Equal(g49,g50)
    c: Equal(g49,g51)
    c: InternalAlignment(g49,g52)
    c: InternalAlignment(g50,g52)
    c: InternalAlignment(g51,g52)
    c: InternalAlignment(g53,g52)
    c: InternalAlignment(g54,g52)
    c: Block(g52)
    c: Weight(g55) = 1
    c: Equal(g55,g56)
    c: Equal(g55,g57)
    c: InternalAlignment(g55,g58)
    c: InternalAlignment(g56,g58)
    c: InternalAlignment(g57,g58)
    c: InternalAlignment(g59,g58)
    c: InternalAlignment(g60,g58)
    c: Block(g58)
    c: Weight(g61) = 1
    c: Equal(g61,g62)
    c: Equal(g61,g63)
    c: InternalAlignment(g61,g64)
    c: InternalAlignment(g62,g64)
    c: InternalAlignment(g63,g64)
    c: InternalAlignment(g65,g64)
    c: InternalAlignment(g66,g64)
    c: Block(g64)
    c: Weight(g67) = 1
    c: Equal(g67,g68)
    c: Equal(g67,g69)
    c: InternalAlignment(g67,g70)
    c: InternalAlignment(g68,g70)
    c: InternalAlignment(g69,g70)
    c: InternalAlignment(g71,g70)
    c: InternalAlignment(g72,g70)
    c: Block(g70)
    c: Weight(g73) = 1
    c: Equal(g73,g74)
    c: Equal(g73,g75)
    c: InternalAlignment(g73,g76)
    c: InternalAlignment(g74,g76)
    c: InternalAlignment(g75,g76)
    c: InternalAlignment(g77,g76)
    c: InternalAlignment(g78,g76)
    c: Weight(g79) = 1
    c: Equal(g79,g80)
    c: Equal(g79,g81)
    c: InternalAlignment(g79,g82)
    c: InternalAlignment(g80,g82)
    c: InternalAlignment(g81,g82)
    c: InternalAlignment(g83,g82)
    c: InternalAlignment(g84,g82)
    c: Block(g76)
    c: Block(g82)
    c: Coincident(g85,g76)
    c: Coincident(g85,g82)
    c: Vertical(g85)
    c: Coincident(g86,g76)
    c: Coincident(g86,g58)
    c: Coincident(g87,g58)
    c: Coincident(g87,g82)
    c: Weight(g88) = 1
    c: Equal(g88,g89)
    c: Equal(g88,g90)
    c: InternalAlignment(g88,g91)
    c: InternalAlignment(g89,g91)
    c: InternalAlignment(g90,g91)
    c: InternalAlignment(g92,g91)
    c: InternalAlignment(g93,g91)
    c: Weight(g94) = 1
    c: Equal(g94,g95)
    c: Equal(g94,g96)
    c: InternalAlignment(g94,g97)
    c: InternalAlignment(g95,g97)
    c: InternalAlignment(g96,g97)
    c: InternalAlignment(g98,g97)
    c: InternalAlignment(g99,g97)
    c: Block(g91)
    c: Block(g97)
    c: Coincident(g100,g91)
    c: Coincident(g100,g97)
    c: Vertical(g100)
    c: Coincident(g101,g91)
    c: Coincident(g101,g52)
    c: Coincident(g102,g52)
    c: Coincident(g102,g97)
    c: Weight(g103) = 1
    c: Equal(g103,g104)
    c: Equal(g103,g105)
    c: InternalAlignment(g103,g106)
    c: InternalAlignment(g104,g106)
    c: InternalAlignment(g105,g106)
    c: InternalAlignment(g107,g106)
    c: InternalAlignment(g108,g106)
    c: Weight(g109) = 1
    c: Equal(g109,g110)
    c: Equal(g109,g111)
    c: InternalAlignment(g109,g112)
    c: InternalAlignment(g110,g112)
    c: InternalAlignment(g111,g112)
    c: InternalAlignment(g113,g112)
    c: InternalAlignment(g114,g112)
    c: Block(g106)
    c: Block(g112)
    c: Coincident(g115,g106)
    c: Coincident(g115,g112)
    c: Vertical(g115)
    c: Coincident(g116,g112)
    c: Coincident(g116,g70)
    c: Coincident(g117,g70)
    c: Coincident(g117,g106)
    c: Weight(g118) = 1
    c: Equal(g118,g119)
    c: Equal(g118,g120)
    c: InternalAlignment(g118,g121)
    c: InternalAlignment(g119,g121)
    c: InternalAlignment(g120,g121)
    c: InternalAlignment(g122,g121)
    c: InternalAlignment(g123,g121)
    c: Weight(g124) = 1
    c: Equal(g124,g125)
    c: Equal(g124,g126)
    c: InternalAlignment(g124,g127)
    c: InternalAlignment(g125,g127)
    c: InternalAlignment(g126,g127)
    c: InternalAlignment(g128,g127)
    c: InternalAlignment(g129,g127)
    c: Block(g121)
    c: Block(g127)
    c: Coincident(g130,g121)
    c: Coincident(g130,g127)
    c: Vertical(g130)
    c: Coincident(g131,g127)
    c: Coincident(g131,g64)
    c: Coincident(g132,g64)
    c: Coincident(g132,g121)
    c: Weight(g133) = 1
    c: Equal(g133,g134)
    c: Equal(g133,g135)
    c: InternalAlignment(g133,g136)
    c: InternalAlignment(g134,g136)
    c: InternalAlignment(g135,g136)
    c: InternalAlignment(g137,g136)
    c: InternalAlignment(g138,g136)
    c: Weight(g139) = 1
    c: Equal(g139,g140)
    c: Equal(g139,g141)
    c: InternalAlignment(g139,g142)
    c: InternalAlignment(g140,g142)
    c: InternalAlignment(g141,g142)
    c: InternalAlignment(g143,g142)
    c: InternalAlignment(g144,g142)
    c: Weight(g145) = 1
    c: Equal(g145,g146)
    c: Equal(g145,g147)
    c: InternalAlignment(g145,g148)
    c: InternalAlignment(g146,g148)
    c: InternalAlignment(g147,g148)
    c: InternalAlignment(g149,g148)
    c: InternalAlignment(g150,g148)
    c: Weight(g151) = 1
    c: Equal(g151,g152)
    c: Equal(g151,g153)
    c: InternalAlignment(g151,g154)
    c: InternalAlignment(g152,g154)
    c: InternalAlignment(g153,g154)
    c: InternalAlignment(g155,g154)
    c: InternalAlignment(g156,g154)
    c: Block(g154)
    c: Block(g148)
    c: Block(g142)
    c: Block(g136)
    c: Coincident(g157,g31)
    c: Coincident(g157,g154)
    c: Coincident(g158,g154)
    c: Coincident(g158,g148)
    c: Horizontal(g158)
    c: Coincident(g159,g148)
    c: Coincident(g159,g31)
    c: Vertical(g159)
    c: Coincident(g160,g25)
    c: Coincident(g160,g142)
    c: Vertical(g160)
    c: Coincident(g161,g142)
    c: Coincident(g161,g136)
    c: Horizontal(g161)
    c: Coincident(g162,g136)
    c: Coincident(g162,g25)
    c: Weight(g163) = 1
    c: Equal(g163,g164)
    c: Equal(g163,g165)
    c: InternalAlignment(g163,g166)
    c: InternalAlignment(g164,g166)
    c: InternalAlignment(g165,g166)
    c: InternalAlignment(g167,g166)
    c: InternalAlignment(g168,g166)
    c: Weight(g169) = 1
    c: Equal(g169,g170)
    c: Equal(g169,g171)
    c: InternalAlignment(g169,g172)
    c: InternalAlignment(g170,g172)
    c: InternalAlignment(g171,g172)
    c: InternalAlignment(g173,g172)
    c: InternalAlignment(g174,g172)
    c: Weight(g175) = 1
    c: Equal(g175,g176)
    c: Equal(g175,g177)
    c: InternalAlignment(g175,g178)
    c: InternalAlignment(g176,g178)
    c: InternalAlignment(g177,g178)
    c: InternalAlignment(g179,g178)
    c: InternalAlignment(g180,g178)
    c: Weight(g181) = 1
    c: Equal(g181,g182)
    c: Equal(g181,g183)
    c: InternalAlignment(g181,g184)
    c: InternalAlignment(g182,g184)
    c: InternalAlignment(g183,g184)
    c: InternalAlignment(g185,g184)
    c: InternalAlignment(g186,g184)
    c: Block(g184)
    c: Block(g178)
    c: Block(g172)
    c: Block(g166)
    c: Coincident(g187,g184)
    c: Coincident(g187,g178)
    c: Horizontal(g187)
    c: Coincident(g188,g178)
    c: Coincident(g188,g13)
    c: Vertical(g188)
    c: Coincident(g189,g19)
    c: Coincident(g189,g172)
    c: Vertical(g189)
    c: Coincident(g190,g172)
    c: Coincident(g190,g166)
    c: Horizontal(g190)
    c: Coincident(g191,g166)
    c: Coincident(g191,g19)
    c: Coincident(g192,g13)
    c: Weight(g193) = 1
    c: Equal(g193,g194)
    c: Equal(g193,g195)
    c: InternalAlignment(g193,g196)
    c: InternalAlignment(g194,g196)
    c: InternalAlignment(g195,g196)
    c: InternalAlignment(g197,g196)
    c: InternalAlignment(g198,g196)
    c: Weight(g199) = 1
    c: Equal(g199,g200)
    c: Equal(g199,g201)
    c: InternalAlignment(g199,g202)
    c: InternalAlignment(g200,g202)
    c: InternalAlignment(g201,g202)
    c: InternalAlignment(g203,g202)
    c: InternalAlignment(g204,g202)
    c: Block(g202)
    c: Block(g196)
    c: Coincident(g205,g202)
    c: Coincident(g205,g37)
    c: Coincident(g206,g37)
    c: Coincident(g206,g196)
    c: Coincident(g207,g196)
    c: Coincident(g207,g202)
    c: Vertical(g207)
    c: Weight(g208) = 1
    c: Equal(g208,g209)
    c: Equal(g208,g210)
    c: InternalAlignment(g208,g211)
    c: InternalAlignment(g209,g211)
    c: InternalAlignment(g210,g211)
    c: InternalAlignment(g212,g211)
    c: InternalAlignment(g213,g211)
    c: Weight(g214) = 1
    c: Equal(g214,g215)
    c: Equal(g214,g216)
    c: InternalAlignment(g214,g217)
    c: InternalAlignment(g215,g217)
    c: InternalAlignment(g216,g217)
    c: InternalAlignment(g218,g217)
    c: InternalAlignment(g219,g217)
    c: Block(g217)
    c: Block(g211)
    c: Coincident(g220,g211)
    c: Coincident(g220,g43)
    c: Coincident(g221,g43)
    c: Coincident(g221,g217)
    c: Coincident(g222,g217)
    c: Coincident(g222,g211)
    c: Vertical(g222)
    c: Horizontal(g223)
    c: Block(g223)
    c: Vertical(g224)
    c: Block(g224)
    c: Block(g225)
    c: Weight(g226) = 1
    c: Equal(g226,g227)
    c: Equal(g226,g228)
    c: InternalAlignment(g226,g229)
    c: InternalAlignment(g227,g229)
    c: InternalAlignment(g228,g229)
    c: InternalAlignment(g230,g229)
    c: InternalAlignment(g231,g229)
    c: Weight(g232) = 1
    c: Equal(g232,g233)
    c: Equal(g232,g234)
    c: InternalAlignment(g232,g235)
    c: InternalAlignment(g233,g235)
    c: InternalAlignment(g234,g235)
    c: InternalAlignment(g236,g235)
    c: InternalAlignment(g237,g235)
    c: Weight(g238) = 1
    c: Equal(g238,g239)
    c: Equal(g238,g240)
    c: InternalAlignment(g238,g241)
    c: InternalAlignment(g239,g241)
    c: InternalAlignment(g240,g241)
    c: InternalAlignment(g242,g241)
    c: InternalAlignment(g243,g241)
    c: Weight(g244) = 1
    c: Equal(g244,g245)
    c: Equal(g244,g246)
    c: InternalAlignment(g244,g247)
    c: InternalAlignment(g245,g247)
    c: InternalAlignment(g246,g247)
    c: InternalAlignment(g248,g247)
    c: InternalAlignment(g249,g247)
    c: Block(g229)
    c: Block(g235)
    c: Block(g241)
    c: Block(g247)
    c: Coincident(g250,g235)
    c: Coincident(g250,g229)
    c: Horizontal(g250)
    c: Block(g192)
    c: Weight(g251) = 1
    c: Equal(g251,g252)
    c: Equal(g251,g253)
    c: InternalAlignment(g251,g254)
    c: InternalAlignment(g252,g254)
    c: InternalAlignment(g253,g254)
    c: InternalAlignment(g255,g254)
    c: InternalAlignment(g256,g254)
    c: Weight(g257) = 1
    c: Equal(g257,g258)
    c: Equal(g257,g259)
    c: InternalAlignment(g257,g260)
    c: InternalAlignment(g258,g260)
    c: InternalAlignment(g259,g260)
    c: InternalAlignment(g261,g260)
    c: InternalAlignment(g262,g260)
    c: Block(g254)
    c: Block(g260)
    c: Coincident(g263,g254)
    c: Coincident(g263,g260)
    c: Weight(g264) = 1
    c: Equal(g264,g265)
    c: Equal(g264,g266)
    c: InternalAlignment(g264,g267)
    c: InternalAlignment(g265,g267)
    c: InternalAlignment(g266,g267)
    c: InternalAlignment(g268,g267)
    c: InternalAlignment(g269,g267)
    c: Weight(g270) = 1
    c: Equal(g270,g271)
    c: Equal(g270,g272)
    c: InternalAlignment(g270,g273)
    c: InternalAlignment(g271,g273)
    c: InternalAlignment(g272,g273)
    c: InternalAlignment(g274,g273)
    c: InternalAlignment(g275,g273)
    c: Weight(g276) = 1
    c: Equal(g276,g277)
    c: Equal(g276,g278)
    c: InternalAlignment(g276,g279)
    c: InternalAlignment(g277,g279)
    c: InternalAlignment(g278,g279)
    c: InternalAlignment(g280,g279)
    c: InternalAlignment(g281,g279)
    c: Block(g279)
    c: Block(g273)
    c: Block(g267)
    c: Coincident(g282,g273)
    c: Coincident(g282,g267)
    c: Coincident(g283,g267)
    c: Coincident(g283,g279)
    c: Vertical(g283)
    c: Coincident(g284,g279)
    c: Coincident(g284,g273)
    c: Horizontal(g284)
    c: Weight(g285) = 1
    c: Equal(g285,g286)
    c: InternalAlignment(g285,g287)
    c: InternalAlignment(g286,g287)
    c: InternalAlignment(g288,g287)
    c: InternalAlignment(g289,g287)
    c: Weight(g290) = 1
    c: InternalAlignment(g291,g293)
    c: InternalAlignment(g292,g293)
    c: InternalAlignment(g294,g293)
    c: InternalAlignment(g295,g293)
    c: Weight(g296) = 1
    c: Equal(g296,g297)
    c: Equal(g296,g298)
    c: InternalAlignment(g296,g299)
    c: InternalAlignment(g297,g299)
    c: InternalAlignment(g298,g299)
    c: InternalAlignment(g300,g299)
    c: InternalAlignment(g301,g299)
    c: Equal(g302,g303)
    c: Equal(g302,g304)
    c: InternalAlignment(g302,g305)
    c: InternalAlignment(g303,g305)
    c: InternalAlignment(g304,g305)
    c: InternalAlignment(g306,g305)
    c: InternalAlignment(g307,g305)
    c: Block(g293)
    c: Block(g299)
    c: Block(g305)
    c: Block(g287)
    c: Coincident(g308,g287)
    c: Coincident(g308,g293)
    c: Horizontal(g308)
    c: Coincident(g309,g293)
    c: Coincident(g309,g299)
    c: Vertical(g309)
    c: Coincident(g310,g299)
    c: Coincident(g310,g305)
    c: Horizontal(g310)
    c: Coincident(g311,g305)
    c: Coincident(g311,g287)
    c: Weight(g312) = 1
    c: Equal(g312,g313)
    c: Equal(g312,g314)
    c: InternalAlignment(g312,g315)
    c: InternalAlignment(g313,g315)
    c: InternalAlignment(g314,g315)
    c: InternalAlignment(g316,g315)
    c: InternalAlignment(g317,g315)
    c: Weight(g318) = 1
    c: Equal(g318,g319)
    c: Equal(g318,g320)
    c: InternalAlignment(g318,g321)
    c: InternalAlignment(g319,g321)
    c: InternalAlignment(g320,g321)
    c: InternalAlignment(g322,g321)
    c: InternalAlignment(g323,g321)
    c: Weight(g324) = 1
    c: Equal(g324,g325)
    c: Equal(g324,g326)
    c: InternalAlignment(g324,g327)
    c: InternalAlignment(g325,g327)
    c: InternalAlignment(g326,g327)
    c: InternalAlignment(g328,g327)
    c: InternalAlignment(g329,g327)
    c: Block(g327)
    c: Block(g321)
    c: Block(g315)
    c: Coincident(g330,g327)
    c: Coincident(g330,g321)
    c: Horizontal(g330)
    c: Coincident(g331,g321)
    c: Coincident(g331,g315)
    c: Vertical(g331)
    c: Coincident(g332,g315)
    c: Coincident(g332,g327)
    c: InternalAlignment(g333,g334)
    c: InternalAlignment(g335,g334)
    c: InternalAlignment(g336,g334)
    c: Block(g334)
    c: Equal(g337,g338)
    c: Equal(g337,g339)
    c: InternalAlignment(g337,g340)
    c: InternalAlignment(g338,g340)
    c: InternalAlignment(g339,g340)
    c: InternalAlignment(g341,g340)
    c: InternalAlignment(g342,g340)
    c: Block(g340)
    c: Coincident(g343,g334)
    c: Horizontal(g343)
    c: Block(g343)
    c: Coincident(g344,g334)
    c: Coincident(g344,g260)
    c: Vertical(g344)
    c: Coincident(g345,g340)
    c: Coincident(g345,g254)
    c: Vertical(g345)
    c: Coincident(g347,g5)
    c: Coincident(g348,g5)
    c: Block(g346)
    c: Block(g5)
    c: Block(g348)
    c: Block(g347)
    c: Distance(g344) = 119.89
FEATURE [Sketcher::SketchObject] Sketch001
  FullyConstrained = true
  MapMode = 4
  Placement = pos=(0,0,0) rot=(0.57735,0.57735,0.57735;2.0944rad)
  Support = -> [Sketch]
  sketch-geometry (46):
    g0: BSplineCurve PolesCount=3 KnotsCount=2 Degree=2 IsPeriodic=0
    g1: ArcOfCircle CenterX=73.1223 CenterY=-32.291 CenterZ=0 NormalX=0 NormalY=0 NormalZ=1 AngleXU=0 Radius=13 StartAngle=5.92268 EndAngle=9.06428
    g2: ArcOfCircle CenterX=66.7816 CenterY=-49.1439 CenterZ=0 NormalX=0 NormalY=0 NormalZ=1 AngleXU=0 Radius=13 StartAngle=2.78068 EndAngle=5.92131
    g3: ArcOfCircle CenterX=55.9263 CenterY=-78.1807 CenterZ=0 NormalX=0 NormalY=0 NormalZ=1 AngleXU=0 Radius=13 StartAngle=5.92268 EndAngle=9.06428
    g4: ArcOfCircle CenterX=49.5884 CenterY=-95.0342 CenterZ=0 NormalX=0 NormalY=0 NormalZ=1 AngleXU=0 Radius=13 StartAngle=2.78068 EndAngle=5.92131
    g5: ArcOfCircle CenterX=38.7206 CenterY=-124.067 CenterZ=0 NormalX=0 NormalY=0 NormalZ=1 AngleXU=0 Radius=13 StartAngle=5.92268 EndAngle=9.06428
    g6: ArcOfCircle CenterX=32.3875 CenterY=-140.92 CenterZ=0 NormalX=0 NormalY=0 NormalZ=1 AngleXU=0 Radius=13 StartAngle=2.78068 EndAngle=5.92131
    g7: ArcOfCircle CenterX=21.4715 CenterY=-169.934 CenterZ=0 NormalX=0 NormalY=0 NormalZ=1 AngleXU=0 Radius=13 StartAngle=5.92268 EndAngle=9.06428
    g8: ArcOfCircle CenterX=15.1336 CenterY=-186.787 CenterZ=0 NormalX=0 NormalY=0 NormalZ=1 AngleXU=0 Radius=13 StartAngle=2.78068 EndAngle=5.92131
    g9-g12: Circle x4 (B-spline internal-alignment scaffolding for g13; pole/knot coordinates omitted)
    g13: BSplineCurve PolesCount=4 KnotsCount=2 Degree=3 IsPeriodic=0
    g14: GeomPoint X=28.8094 Y=-19.0875 Z=0
    g15: GeomPoint X=47.0443 Y=-50.4712 Z=0
    g16: Circle CenterX=53.5586 CenterY=-23.2695 CenterZ=0 NormalX=0 NormalY=0 NormalZ=1 AngleXU=0 Radius=3.24518
    g17: Circle CenterX=-195.441 CenterY=-127.082 CenterZ=0 NormalX=0 NormalY=0 NormalZ=1 AngleXU=0 Radius=1
    g18: Circle CenterX=-8.24091 CenterY=-197.481 CenterZ=0 NormalX=0 NormalY=0 NormalZ=1 AngleXU=0 Radius=1
    g19: Circle CenterX=12.8789 CenterY=-141.321 CenterZ=0 NormalX=0 NormalY=0 NormalZ=1 AngleXU=0 Radius=1
    g20: BSplineCurve PolesCount=3 KnotsCount=2 Degree=2 IsPeriodic=0
    g21: GeomPoint X=-195.441 Y=-127.082 Z=0
    g22: GeomPoint X=12.8789 Y=-141.321 Z=0
    g23: Circle CenterX=-12.8016 CenterY=-179.036 CenterZ=0 NormalX=0 NormalY=0 NormalZ=1 AngleXU=0 Radius=10.5072
    g24: Circle CenterX=0.933922 CenterY=-166.43 CenterZ=0 NormalX=0 NormalY=0 NormalZ=1 AngleXU=0 Radius=3.26661
    g25: Circle CenterX=-33.5518 CenterY=-176.44 CenterZ=0 NormalX=0 NormalY=0 NormalZ=1 AngleXU=0 Radius=5.64388
    g26: Circle CenterX=-47.2366 CenterY=-173.859 CenterZ=0 NormalX=0 NormalY=0 NormalZ=1 AngleXU=0 Radius=3.01653
    g27: Circle CenterX=-56.2595 CenterY=-171.456 CenterZ=0 NormalX=0 NormalY=0 NormalZ=1 AngleXU=0 Radius=2.12826
    g28: ArcOfCircle CenterX=51.2151 CenterY=-198.473 CenterZ=0 NormalX=0 NormalY=0 NormalZ=1 AngleXU=0 Radius=20 StartAngle=2.78189 EndAngle=4.35269
    g29: LineSegment StartX=32.4951 StartY=-191.433 StartZ=0 EndX=94.6578 EndY=-26.1352 EndZ=0
    g30: LineSegment StartX=43.1192 StartY=-220.001 StartZ=0 EndX=-196.497 EndY=-129.89 EndZ=0
    g31: LineSegment StartX=43.1192 StartY=-220.001 StartZ=0 EndX=44.1752 EndY=-217.193 EndZ=0
    g32: LineSegment StartX=117.223 StartY=-19.0875 StartZ=0 EndX=117.223 EndY=-16.0875 EndZ=0
    g33: LineSegment StartX=117.223 StartY=-16.0875 StartZ=0 EndX=17.2232 EndY=-16.0875 EndZ=0
    g34: LineSegment StartX=17.2232 StartY=-16.0875 StartZ=0 EndX=17.2232 EndY=-19.0875 EndZ=0
    g35: LineSegment StartX=28.8094 StartY=-19.0875 StartZ=0 EndX=17.2232 EndY=-19.0875 EndZ=0
    g36: LineSegment StartX=47.0443 StartY=-50.4712 StartZ=0 EndX=12.8789 EndY=-141.321 EndZ=0
    g37: LineSegment StartX=-195.441 StartY=-127.082 StartZ=0 EndX=-196.497 EndY=-129.89 EndZ=0
    g38: LineSegment StartX=85.2866 StartY=-36.8766 StartZ=0 EndX=78.9396 EndY=-53.7463 EndZ=0
    g39: LineSegment StartX=60.9579 StartY=-27.7053 StartZ=0 EndX=54.6191 EndY=-44.5532 EndZ=0
    g40: LineSegment StartX=68.0907 StartY=-82.7664 StartZ=0 EndX=61.7465 EndY=-99.6365 EndZ=0
    g41: LineSegment StartX=43.7619 StartY=-73.595 StartZ=0 EndX=37.426 EndY=-90.4435 EndZ=0
    g42: LineSegment StartX=50.885 StartY=-128.652 StartZ=0 EndX=44.5456 EndY=-145.522 EndZ=0
    g43: LineSegment StartX=26.5562 StartY=-119.481 StartZ=0 EndX=20.2251 EndY=-136.329 EndZ=0
    g44: LineSegment StartX=9.3071 StartY=-165.349 StartZ=0 EndX=2.97115 EndY=-182.197 EndZ=0
    g45: LineSegment StartX=33.6358 StartY=-174.52 StartZ=0 EndX=27.2917 EndY=-191.39 EndZ=0
  constraints (71):
    c: Block(g0)
    c: Block(g1)
    c: Block(g2)
    c: Block(g4)
    c: Block(g3)
    c: Block(g6)
    c: Block(g5)
    c: Block(g8)
    c: Block(g7)
    c: Weight(g9) = 1
    c: Equal(g9,g10)
    c: Equal(g9,g11)
    c: Equal(g9,g12)
    c: InternalAlignment(g9-g12 -> g13) x4
    c: InternalAlignment(g14,g13)
    c: InternalAlignment(g15,g13)
    c: Block(g16)
    c: Weight(g17) = 1
    c: Equal(g17,g18)
    c: Equal(g17,g19)
    c: InternalAlignment(g17,g20)
    c: InternalAlignment(g18,g20)
    c: InternalAlignment(g19,g20)
    c: InternalAlignment(g21,g20)
    c: InternalAlignment(g22,g20)
    c: Block(g20)
    c: Block(g23)
    c: Block(g24)
    c: Block(g25)
    c: Block(g26)
    c: Block(g27)
    c: Block(g28)
    c: Coincident(g29,g28)
    c: Coincident(g29,g0)
    c: Block(g13)
    c: Coincident(g31,g30)
    c: Coincident(g31,g28)
    c: Block(g31)
    c: Coincident(g32,g0)
    c: Vertical(g32)
    c: Coincident(g33,g32)
    c: Horizontal(g33)
    c: Coincident(g34,g33)
    c: Vertical(g34)
    c: Block(g33)
    c: Coincident(g35,g13)
    c: Coincident(g35,g34)
    c: Horizontal(g35)
    c: Coincident(g36,g13)
    c: Coincident(g36,g20)
    c: Coincident(g37,g20)
    c: Coincident(g37,g30)
    c: Block(g30)
    c: Coincident(g38,g1)
    c: Coincident(g38,g2)
    c: Coincident(g39,g1)
    c: Coincident(g39,g2)
    c: Coincident(g40,g3)
    c: Coincident(g40,g4)
    c: Coincident(g41,g3)
    c: Coincident(g41,g4)
    c: Coincident(g42,g5)
    c: Coincident(g42,g6)
    c: Coincident(g43,g5)
    c: Coincident(g43,g6)
    c: Coincident(g44,g7)
    c: Coincident(g44,g8)
    c: Coincident(g45,g7)
    c: Coincident(g45,g8)
    c: Distance(g30) = 256
    c: Distance(g33) = 100
FEATURE [Part::Extrusion] Extrude002
  Base = -> Sketch001
  Dir = (1,0,0)
  DirMode = 2
  FaceMakerClass = Part::FaceMakerBullseye
  LengthFwd = 8
  LengthRev = 0
  Solid = true
  Symmetric = false
FEATURE [Sketcher::SketchObject] Sketch002
  FullyConstrained = true
  sketch-geometry (20):
    g0: LineSegment StartX=-2.77179 StartY=-200.304 StartZ=0 EndX=5.22821 EndY=-200.304 EndZ=0
    g1: LineSegment StartX=5.22821 StartY=-200.304 StartZ=0 EndX=5.22821 EndY=-197.304 EndZ=0
    g2: LineSegment StartX=-2.77179 StartY=-200.304 StartZ=0 EndX=-2.77179 EndY=-197.304 EndZ=0
    g3: LineSegment StartX=5.22821 StartY=-197.304 StartZ=0 EndX=8.22821 EndY=-197.304 EndZ=0
    g4: LineSegment StartX=-2.77179 StartY=-197.304 StartZ=0 EndX=-5.77179 EndY=-197.304 EndZ=0
    g5: LineSegment StartX=19.2282 StartY=-203.304 StartZ=0 EndX=19.2282 EndY=-206.304 EndZ=0
    g6: LineSegment StartX=-16.7718 StartY=-203.304 StartZ=0 EndX=-16.7718 EndY=-206.304 EndZ=0
    g7: LineSegment StartX=-16.7718 StartY=-206.304 StartZ=0 EndX=19.2282 EndY=-206.304 EndZ=0
    g8: Circle CenterX=-16.7718 CenterY=-203.304 CenterZ=0 NormalX=0 NormalY=0 NormalZ=1 AngleXU=0 Radius=1
    g9: Circle CenterX=-5.77179 CenterY=-203.304 CenterZ=0 NormalX=0 NormalY=0 NormalZ=1 AngleXU=0 Radius=1
    g10: Circle CenterX=-5.77179 CenterY=-197.304 CenterZ=0 NormalX=0 NormalY=0 NormalZ=1 AngleXU=0 Radius=1
    g11: BSplineCurve PolesCount=3 KnotsCount=2 Degree=2 IsPeriodic=0
    g12: GeomPoint X=-16.7718 Y=-203.304 Z=0
    g13: GeomPoint X=-5.77179 Y=-197.304 Z=0
    g14: Circle CenterX=19.2282 CenterY=-203.304 CenterZ=0 NormalX=0 NormalY=0 NormalZ=1 AngleXU=0 Radius=1
    g15: Circle CenterX=8.22821 CenterY=-203.304 CenterZ=0 NormalX=0 NormalY=0 NormalZ=1 AngleXU=0 Radius=1
    g16: Circle CenterX=8.22821 CenterY=-197.304 CenterZ=0 NormalX=0 NormalY=0 NormalZ=1 AngleXU=0 Radius=1
    g17: BSplineCurve PolesCount=3 KnotsCount=2 Degree=2 IsPeriodic=0
    g18: GeomPoint X=19.2282 Y=-203.304 Z=0
    g19: GeomPoint X=8.22821 Y=-197.304 Z=0
  constraints (41):
    c: Horizontal(g0)
    c: Distance(g0) = 8
    c: Coincident(g1,g0)
    c: Vertical(g1)
    c: Distance(g1) = 3
    c: Coincident(g2,g0)
    c: Vertical(g2)
    c: Distance(g2) = 3
    c: Coincident(g3,g1)
    c: Horizontal(g3)
    c: Distance(g3) = 3
    c: Coincident(g4,g2)
    c: Horizontal(g4)
    c: Distance(g4) = 3
    c: Vertical(g5)
    c: Vertical(g6)
    c: Coincident(g7,g6)
    c: Coincident(g7,g5)
    c: Weight(g8) = 1
    c: Equal(g8,g9)
    c: Equal(g8,g10)
    c: Coincident(g11,g4)
    c: InternalAlignment(g8,g11)
    c: InternalAlignment(g9,g11)
    c: InternalAlignment(g10,g11)
    c: InternalAlignment(g12,g11)
    c: InternalAlignment(g13,g11)
    c: Coincident(g17,g5)
    c: Weight(g14) = 1
    c: Equal(g14,g15)
    c: Equal(g14,g16)
    c: Coincident(g17,g3)
    c: InternalAlignment(g14,g17)
    c: InternalAlignment(g15,g17)
    c: InternalAlignment(g16,g17)
    c: InternalAlignment(g18,g17)
    c: InternalAlignment(g19,g17)
    c: Block(g7)
    c: Block(g17)
    c: Block(g11)
    c: Block(g6)
FEATURE [Part::Extrusion] Extrude003
  Base = -> Sketch002
  Dir = (0,0,1)
  DirMode = 2
  FaceMakerClass = Part::FaceMakerBullseye
  LengthFwd = 260
  LengthRev = 0
  Solid = true
  Symmetric = false
FEATURE [Part::Extrusion] Extrude
  Base = -> Sketch
  Dir = (0,0,1)
  DirMode = 2
  FaceMakerClass = Part::FaceMakerBullseye
  LengthFwd = 14
  LengthRev = 0
  Solid = true
  Symmetric = false
FEATURE [Sketcher::SketchObject] Sketch003
  FullyConstrained = false
  sketch-geometry (357):
    g0: LineSegment StartX=-10.9272 StartY=-82.7794 StartZ=0 EndX=46.0728 EndY=-51.4823 EndZ=0
    g1: LineSegment StartX=-10.9272 StartY=76.4095 StartZ=0 EndX=-10.9272 EndY=-82.7794 EndZ=0
    g2: LineSegment StartX=46.0728 StartY=76.4095 StartZ=0 EndX=46.0728 EndY=-51.4823 EndZ=0
    g3: LineSegment StartX=-42.9272 StartY=136.221 StartZ=0 EndX=-42.9272 EndY=-103.779 EndZ=0
    g4: LineSegment StartX=407.073 StartY=136.221 StartZ=0 EndX=407.073 EndY=-103.779 EndZ=0
    g5: ArcOfCircle CenterX=-26.9272 CenterY=-83.7794 CenterZ=0 NormalX=0 NormalY=0 NormalZ=1 AngleXU=0 Radius=8 StartAngle=3.14159 EndAngle=6.28319
    g6: ArcOfCircle CenterX=391.073 CenterY=-83.7794 CenterZ=0 NormalX=0 NormalY=0 NormalZ=1 AngleXU=0 Radius=8 StartAngle=3.14159 EndAngle=6.28319
    g7: Circle CenterX=175.022 CenterY=27.0628 CenterZ=0 NormalX=0 NormalY=0 NormalZ=1 AngleXU=0 Radius=1
    g8: Circle CenterX=179.022 CenterY=24.8665 CenterZ=0 NormalX=0 NormalY=0 NormalZ=1 AngleXU=0 Radius=1
    g9: Circle CenterX=179.022 CenterY=27.0628 CenterZ=0 NormalX=0 NormalY=0 NormalZ=1 AngleXU=0 Radius=1
    g10: BSplineCurve PolesCount=3 KnotsCount=2 Degree=2 IsPeriodic=0
    g11: GeomPoint X=175.022 Y=27.0628 Z=0
    g12: GeomPoint X=179.022 Y=27.0628 Z=0
    g13: Circle CenterX=189.124 CenterY=27.0628 CenterZ=0 NormalX=0 NormalY=0 NormalZ=1 AngleXU=0 Radius=1
    g14: Circle CenterX=185.124 CenterY=24.8665 CenterZ=0 NormalX=0 NormalY=0 NormalZ=1 AngleXU=0 Radius=1
    g15: Circle CenterX=185.124 CenterY=27.0628 CenterZ=0 NormalX=0 NormalY=0 NormalZ=1 AngleXU=0 Radius=1
    g16: BSplineCurve PolesCount=3 KnotsCount=2 Degree=2 IsPeriodic=0
    g17: GeomPoint X=189.124 Y=27.0628 Z=0
    g18: GeomPoint X=185.124 Y=27.0628 Z=0
    g19: Circle CenterX=175.022 CenterY=5.37834 CenterZ=0 NormalX=0 NormalY=0 NormalZ=1 AngleXU=0 Radius=1
    g20: Circle CenterX=179.022 CenterY=7.57463 CenterZ=0 NormalX=0 NormalY=0 NormalZ=1 AngleXU=0 Radius=1
    g21: Circle CenterX=179.022 CenterY=5.34704 CenterZ=0 NormalX=0 NormalY=0 NormalZ=1 AngleXU=0 Radius=1
    g22: BSplineCurve PolesCount=3 KnotsCount=2 Degree=2 IsPeriodic=0
    g23: GeomPoint X=175.022 Y=5.37834 Z=0
    g24: GeomPoint X=179.022 Y=5.34704 Z=0
    g25: Circle CenterX=189.124 CenterY=5.37834 CenterZ=0 NormalX=0 NormalY=0 NormalZ=1 AngleXU=0 Radius=1
    g26: Circle CenterX=185.124 CenterY=7.57463 CenterZ=0 NormalX=0 NormalY=0 NormalZ=1 AngleXU=0 Radius=1
    g27: Circle CenterX=185.124 CenterY=5.34704 CenterZ=0 NormalX=0 NormalY=0 NormalZ=1 AngleXU=0 Radius=1
    g28: BSplineCurve PolesCount=3 KnotsCount=2 Degree=2 IsPeriodic=0
    g29: GeomPoint X=189.124 Y=5.37834 Z=0
    g30: GeomPoint X=185.124 Y=5.34704 Z=0
    g31: Circle CenterX=165.871 CenterY=18.1458 CenterZ=0 NormalX=0 NormalY=0 NormalZ=1 AngleXU=0 Radius=1
    g32: Circle CenterX=169.377 CenterY=16.2206 CenterZ=0 NormalX=0 NormalY=0 NormalZ=1 AngleXU=0 Radius=1
    g33: Circle CenterX=165.871 CenterY=14.2954 CenterZ=0 NormalX=0 NormalY=0 NormalZ=1 AngleXU=0 Radius=1
    g34: BSplineCurve PolesCount=3 KnotsCount=2 Degree=2 IsPeriodic=0
    g35: GeomPoint X=165.871 Y=18.1458 Z=0
    g36: GeomPoint X=165.871 Y=14.2954 Z=0
    g37: Circle CenterX=198.275 CenterY=18.1458 CenterZ=0 NormalX=0 NormalY=0 NormalZ=1 AngleXU=0 Radius=1
    g38: Circle CenterX=194.768 CenterY=16.2206 CenterZ=0 NormalX=0 NormalY=0 NormalZ=1 AngleXU=0 Radius=1
    g39: Circle CenterX=198.275 CenterY=14.2954 CenterZ=0 NormalX=0 NormalY=0 NormalZ=1 AngleXU=0 Radius=1
    g40: BSplineCurve PolesCount=3 KnotsCount=2 Degree=2 IsPeriodic=0
    g41: GeomPoint X=198.275 Y=18.1458 Z=0
    g42: GeomPoint X=198.275 Y=14.2954 Z=0
    g43: LineSegment StartX=407.073 StartY=-103.779 StartZ=0 EndX=-42.9272 EndY=-103.779 EndZ=0
    g44: LineSegment StartX=407.073 StartY=136.221 StartZ=0 EndX=-42.9272 EndY=136.221 EndZ=0
    g45: LineSegment StartX=46.0728 StartY=76.4095 StartZ=0 EndX=-10.9272 EndY=76.4095 EndZ=0
    g46: Circle CenterX=125.607 CenterY=54.1951 CenterZ=0 NormalX=0 NormalY=0 NormalZ=1 AngleXU=0 Radius=1
    g47: Circle CenterX=139.632 CenterY=46.4944 CenterZ=0 NormalX=0 NormalY=0 NormalZ=1 AngleXU=0 Radius=1
    g48: Circle CenterX=127.326 CenterY=56.7187 CenterZ=0 NormalX=0 NormalY=0 NormalZ=1 AngleXU=0 Radius=1
    g49: BSplineCurve PolesCount=3 KnotsCount=2 Degree=2 IsPeriodic=0
    g50: GeomPoint X=125.607 Y=54.1951 Z=0
    g51: GeomPoint X=127.326 Y=56.7187 Z=0
    g52: Circle CenterX=236.821 CenterY=56.7187 CenterZ=0 NormalX=0 NormalY=0 NormalZ=1 AngleXU=0 Radius=1
    g53: Circle CenterX=224.513 CenterY=46.4944 CenterZ=0 NormalX=0 NormalY=0 NormalZ=1 AngleXU=0 Radius=1
    g54: Circle CenterX=238.538 CenterY=54.1951 CenterZ=0 NormalX=0 NormalY=0 NormalZ=1 AngleXU=0 Radius=1
    g55: BSplineCurve PolesCount=3 KnotsCount=2 Degree=2 IsPeriodic=0
    g56: GeomPoint X=236.821 Y=56.7187 Z=0
    g57: GeomPoint X=238.538 Y=54.1951 Z=0
    g58: Circle CenterX=238.538 CenterY=-21.7539 CenterZ=0 NormalX=0 NormalY=0 NormalZ=1 AngleXU=0 Radius=1
    g59: Circle CenterX=224.513 CenterY=-14.0532 CenterZ=0 NormalX=0 NormalY=0 NormalZ=1 AngleXU=0 Radius=1
    g60: Circle CenterX=236.821 CenterY=-24.2775 CenterZ=0 NormalX=0 NormalY=0 NormalZ=1 AngleXU=0 Radius=1
    g61: BSplineCurve PolesCount=3 KnotsCount=2 Degree=2 IsPeriodic=0
    g62: GeomPoint X=238.538 Y=-21.7539 Z=0
    g63: GeomPoint X=236.821 Y=-24.2775 Z=0
    g64: Circle CenterX=125.607 CenterY=-21.7539 CenterZ=0 NormalX=0 NormalY=0 NormalZ=1 AngleXU=0 Radius=1
    g65: Circle CenterX=139.632 CenterY=-14.0532 CenterZ=0 NormalX=0 NormalY=0 NormalZ=1 AngleXU=0 Radius=1
    g66: Circle CenterX=127.325 CenterY=-24.2775 CenterZ=0 NormalX=0 NormalY=0 NormalZ=1 AngleXU=0 Radius=1
    g67: BSplineCurve PolesCount=3 KnotsCount=2 Degree=2 IsPeriodic=0
    g68: GeomPoint X=125.607 Y=-21.7539 Z=0
    g69: GeomPoint X=127.325 Y=-24.2775 Z=0
    g70: Circle CenterX=302.996 CenterY=111.695 CenterZ=0 NormalX=0 NormalY=0 NormalZ=1 AngleXU=0 Radius=1
    g71: Circle CenterX=306.073 CenterY=114.251 CenterZ=0 NormalX=0 NormalY=0 NormalZ=1 AngleXU=0 Radius=1
    g72: Circle CenterX=306.073 CenterY=110.251 CenterZ=0 NormalX=0 NormalY=0 NormalZ=1 AngleXU=0 Radius=1
    g73: BSplineCurve PolesCount=3 KnotsCount=2 Degree=2 IsPeriodic=0
    g74: GeomPoint X=302.996 Y=111.695 Z=0
    g75: GeomPoint X=306.073 Y=110.251 Z=0
    g76: Circle CenterX=306.073 CenterY=95.2763 CenterZ=0 NormalX=0 NormalY=0 NormalZ=1 AngleXU=0 Radius=1
    g77: Circle CenterX=306.073 CenterY=91.2763 CenterZ=0 NormalX=0 NormalY=0 NormalZ=1 AngleXU=0 Radius=1
    g78: Circle CenterX=302.567 CenterY=89.3511 CenterZ=0 NormalX=0 NormalY=0 NormalZ=1 AngleXU=0 Radius=1
    g79: BSplineCurve PolesCount=3 KnotsCount=2 Degree=2 IsPeriodic=0
    g80: GeomPoint X=306.073 Y=95.2763 Z=0
    g81: GeomPoint X=302.567 Y=89.3511 Z=0
    g82: LineSegment StartX=306.073 StartY=110.251 StartZ=0 EndX=306.073 EndY=95.2763 EndZ=0
    g83: LineSegment StartX=302.996 StartY=111.695 StartZ=0 EndX=236.821 EndY=56.7187 EndZ=0
    g84: LineSegment StartX=238.538 StartY=54.1951 StartZ=0 EndX=302.567 EndY=89.3511 EndZ=0
    g85: Circle CenterX=61.1496 CenterY=111.695 CenterZ=0 NormalX=0 NormalY=0 NormalZ=1 AngleXU=0 Radius=1
    g86: Circle CenterX=58.0728 CenterY=114.251 CenterZ=0 NormalX=0 NormalY=0 NormalZ=1 AngleXU=0 Radius=1
    g87: Circle CenterX=58.0728 CenterY=110.251 CenterZ=0 NormalX=0 NormalY=0 NormalZ=1 AngleXU=0 Radius=1
    g88: BSplineCurve PolesCount=3 KnotsCount=2 Degree=2 IsPeriodic=0
    g89: GeomPoint X=61.1496 Y=111.695 Z=0
    g90: GeomPoint X=58.0728 Y=110.251 Z=0
    g91: Circle CenterX=61.5791 CenterY=89.3511 CenterZ=0 NormalX=0 NormalY=0 NormalZ=1 AngleXU=0 Radius=1
    g92: Circle CenterX=58.0728 CenterY=91.2763 CenterZ=0 NormalX=0 NormalY=0 NormalZ=1 AngleXU=0 Radius=1
    g93: Circle CenterX=58.0728 CenterY=95.2763 CenterZ=0 NormalX=0 NormalY=0 NormalZ=1 AngleXU=0 Radius=1
    g94: BSplineCurve PolesCount=3 KnotsCount=2 Degree=2 IsPeriodic=0
    g95: GeomPoint X=61.5791 Y=89.3511 Z=0
    g96: GeomPoint X=58.0728 Y=95.2763 Z=0
    g97: LineSegment StartX=58.0728 StartY=110.251 StartZ=0 EndX=58.0728 EndY=95.2763 EndZ=0
    g98: LineSegment StartX=61.1496 StartY=111.695 StartZ=0 EndX=127.326 EndY=56.7187 EndZ=0
    g99: LineSegment StartX=125.607 StartY=54.1951 StartZ=0 EndX=61.5791 EndY=89.3511 EndZ=0
    g100: Circle CenterX=61.5791 CenterY=-56.9099 CenterZ=0 NormalX=0 NormalY=0 NormalZ=1 AngleXU=0 Radius=1
    g101: Circle CenterX=58.0728 CenterY=-58.8351 CenterZ=0 NormalX=0 NormalY=0 NormalZ=1 AngleXU=0 Radius=1
    g102: Circle CenterX=58.0728 CenterY=-62.8351 CenterZ=0 NormalX=0 NormalY=0 NormalZ=1 AngleXU=0 Radius=1
    g103: BSplineCurve PolesCount=3 KnotsCount=2 Degree=2 IsPeriodic=0
    g104: GeomPoint X=61.5791 Y=-56.9099 Z=0
    g105: GeomPoint X=58.0728 Y=-62.8351 Z=0
    g106: Circle CenterX=58.0728 CenterY=-77.8102 CenterZ=0 NormalX=0 NormalY=0 NormalZ=1 AngleXU=0 Radius=1
    g107: Circle CenterX=58.0728 CenterY=-81.8102 CenterZ=0 NormalX=0 NormalY=0 NormalZ=1 AngleXU=0 Radius=1
    g108: Circle CenterX=61.1496 CenterY=-79.2541 CenterZ=0 NormalX=0 NormalY=0 NormalZ=1 AngleXU=0 Radius=1
    g109: BSplineCurve PolesCount=3 KnotsCount=2 Degree=2 IsPeriodic=0
    g110: GeomPoint X=58.0728 Y=-77.8102 Z=0
    g111: GeomPoint X=61.1496 Y=-79.2541 Z=0
    g112: LineSegment StartX=58.0728 StartY=-62.8351 StartZ=0 EndX=58.0728 EndY=-77.8102 EndZ=0
    g113: LineSegment StartX=61.1496 StartY=-79.2541 StartZ=0 EndX=127.325 EndY=-24.2775 EndZ=0
    g114: LineSegment StartX=125.607 StartY=-21.7539 StartZ=0 EndX=61.5791 EndY=-56.9099 EndZ=0
    g115: Circle CenterX=302.567 CenterY=-56.9099 CenterZ=0 NormalX=0 NormalY=0 NormalZ=1 AngleXU=0 Radius=1
    g116: Circle CenterX=306.073 CenterY=-58.8351 CenterZ=0 NormalX=0 NormalY=0 NormalZ=1 AngleXU=0 Radius=1
    g117: Circle CenterX=306.073 CenterY=-62.8351 CenterZ=0 NormalX=0 NormalY=0 NormalZ=1 AngleXU=0 Radius=1
    g118: BSplineCurve PolesCount=3 KnotsCount=2 Degree=2 IsPeriodic=0
    g119: GeomPoint X=302.567 Y=-56.9099 Z=0
    g120: GeomPoint X=306.073 Y=-62.8351 Z=0
    g121: Circle CenterX=302.996 CenterY=-79.2541 CenterZ=0 NormalX=0 NormalY=0 NormalZ=1 AngleXU=0 Radius=1
    g122: Circle CenterX=306.073 CenterY=-81.8102 CenterZ=0 NormalX=0 NormalY=0 NormalZ=1 AngleXU=0 Radius=1
    g123: Circle CenterX=306.073 CenterY=-77.8102 CenterZ=0 NormalX=0 NormalY=0 NormalZ=1 AngleXU=0 Radius=1
    g124: BSplineCurve PolesCount=3 KnotsCount=2 Degree=2 IsPeriodic=0
    g125: GeomPoint X=302.996 Y=-79.2541 Z=0
    g126: GeomPoint X=306.073 Y=-77.8102 Z=0
    g127: LineSegment StartX=306.073 StartY=-62.8351 StartZ=0 EndX=306.073 EndY=-77.8102 EndZ=0
    g128: LineSegment StartX=302.996 StartY=-79.2541 StartZ=0 EndX=236.821 EndY=-24.2775 EndZ=0
    g129: LineSegment StartX=238.538 StartY=-21.7539 StartZ=0 EndX=302.567 EndY=-56.9099 EndZ=0
    g130: Circle CenterX=61.6457 CenterY=-88.8112 CenterZ=0 NormalX=0 NormalY=0 NormalZ=1 AngleXU=0 Radius=1
    g131: Circle CenterX=58.0728 CenterY=-91.7794 CenterZ=0 NormalX=0 NormalY=0 NormalZ=1 AngleXU=0 Radius=1
    g132: Circle CenterX=63.9135 CenterY=-91.7794 CenterZ=0 NormalX=0 NormalY=0 NormalZ=1 AngleXU=0 Radius=1
    g133: BSplineCurve PolesCount=3 KnotsCount=2 Degree=2 IsPeriodic=0
    g134: GeomPoint X=61.6457 Y=-88.8112 Z=0
    g135: GeomPoint X=63.9135 Y=-91.7794 Z=0
    g136: Circle CenterX=179.022 CenterY=-85.8163 CenterZ=0 NormalX=0 NormalY=0 NormalZ=1 AngleXU=0 Radius=1
    g137: Circle CenterX=179.022 CenterY=-91.7794 CenterZ=0 NormalX=0 NormalY=0 NormalZ=1 AngleXU=0 Radius=1
    g138: Circle CenterX=171.895 CenterY=-91.7794 CenterZ=0 NormalX=0 NormalY=0 NormalZ=1 AngleXU=0 Radius=1
    g139: BSplineCurve PolesCount=3 KnotsCount=2 Degree=2 IsPeriodic=0
    g140: GeomPoint X=179.022 Y=-85.8163 Z=0
    g141: GeomPoint X=171.895 Y=-91.7794 Z=0
    g142: Circle CenterX=185.124 CenterY=-86.2028 CenterZ=0 NormalX=0 NormalY=0 NormalZ=1 AngleXU=0 Radius=1
    g143: Circle CenterX=185.124 CenterY=-91.7794 CenterZ=0 NormalX=0 NormalY=0 NormalZ=1 AngleXU=0 Radius=1
    g144: Circle CenterX=191.747 CenterY=-91.7794 CenterZ=0 NormalX=0 NormalY=0 NormalZ=1 AngleXU=0 Radius=1
    g145: BSplineCurve PolesCount=3 KnotsCount=2 Degree=2 IsPeriodic=0
    g146: GeomPoint X=185.124 Y=-86.2028 Z=0
    g147: GeomPoint X=191.747 Y=-91.7794 Z=0
    g148: Circle CenterX=299.888 CenterY=-86.6413 CenterZ=0 NormalX=0 NormalY=0 NormalZ=1 AngleXU=0 Radius=1
    g149: Circle CenterX=306.073 CenterY=-91.7794 CenterZ=0 NormalX=0 NormalY=0 NormalZ=1 AngleXU=0 Radius=1
    g150: Circle CenterX=298.776 CenterY=-91.7794 CenterZ=0 NormalX=0 NormalY=0 NormalZ=1 AngleXU=0 Radius=1
    g151: BSplineCurve PolesCount=3 KnotsCount=2 Degree=2 IsPeriodic=0
    g152: GeomPoint X=299.888 Y=-86.6413 Z=0
    g153: GeomPoint X=298.776 Y=-91.7794 Z=0
    g154: LineSegment StartX=189.124 StartY=5.37834 StartZ=0 EndX=299.888 EndY=-86.6413 EndZ=0
    g155: LineSegment StartX=298.776 StartY=-91.7794 StartZ=0 EndX=191.747 EndY=-91.7794 EndZ=0
    g156: LineSegment StartX=185.124 StartY=-86.2028 StartZ=0 EndX=185.124 EndY=5.34704 EndZ=0
    g157: LineSegment StartX=179.022 StartY=5.34704 StartZ=0 EndX=179.022 EndY=-85.8163 EndZ=0
    g158: LineSegment StartX=171.895 StartY=-91.7794 StartZ=0 EndX=63.9135 EndY=-91.7794 EndZ=0
    g159: LineSegment StartX=61.6457 StartY=-88.8112 StartZ=0 EndX=175.022 EndY=5.37834 EndZ=0
    g160: Circle CenterX=302.073 CenterY=124.221 CenterZ=0 NormalX=0 NormalY=0 NormalZ=1 AngleXU=0 Radius=1
    g161: Circle CenterX=306.073 CenterY=124.221 CenterZ=0 NormalX=0 NormalY=0 NormalZ=1 AngleXU=0 Radius=1
    g162: Circle CenterX=302.996 CenterY=121.665 CenterZ=0 NormalX=0 NormalY=0 NormalZ=1 AngleXU=0 Radius=1
    g163: BSplineCurve PolesCount=3 KnotsCount=2 Degree=2 IsPeriodic=0
    g164: GeomPoint X=302.073 Y=124.221 Z=0
    g165: GeomPoint X=302.996 Y=121.665 Z=0
    g166: Circle CenterX=189.124 CenterY=124.221 CenterZ=0 NormalX=0 NormalY=0 NormalZ=1 AngleXU=0 Radius=1
    g167: Circle CenterX=185.124 CenterY=124.221 CenterZ=0 NormalX=0 NormalY=0 NormalZ=1 AngleXU=0 Radius=1
    g168: Circle CenterX=185.124 CenterY=120.221 CenterZ=0 NormalX=0 NormalY=0 NormalZ=1 AngleXU=0 Radius=1
    g169: BSplineCurve PolesCount=3 KnotsCount=2 Degree=2 IsPeriodic=0
    g170: GeomPoint X=189.124 Y=124.221 Z=0
    g171: GeomPoint X=185.124 Y=120.221 Z=0
    g172: Circle CenterX=175.022 CenterY=124.221 CenterZ=0 NormalX=0 NormalY=0 NormalZ=1 AngleXU=0 Radius=1
    g173: Circle CenterX=179.022 CenterY=124.221 CenterZ=0 NormalX=0 NormalY=0 NormalZ=1 AngleXU=0 Radius=1
    g174: Circle CenterX=179.022 CenterY=120.221 CenterZ=0 NormalX=0 NormalY=0 NormalZ=1 AngleXU=0 Radius=1
    g175: BSplineCurve PolesCount=3 KnotsCount=2 Degree=2 IsPeriodic=0
    g176: GeomPoint X=175.022 Y=124.221 Z=0
    g177: GeomPoint X=179.022 Y=120.221 Z=0
    g178: Circle CenterX=62.0728 CenterY=124.221 CenterZ=0 NormalX=0 NormalY=0 NormalZ=1 AngleXU=0 Radius=1
    g179: Circle CenterX=58.0728 CenterY=124.221 CenterZ=0 NormalX=0 NormalY=0 NormalZ=1 AngleXU=0 Radius=1
    g180: Circle CenterX=61.1496 CenterY=121.665 CenterZ=0 NormalX=0 NormalY=0 NormalZ=1 AngleXU=0 Radius=1
    g181: BSplineCurve PolesCount=3 KnotsCount=2 Degree=2 IsPeriodic=0
    g182: GeomPoint X=62.0728 Y=124.221 Z=0
    g183: GeomPoint X=61.1496 Y=121.665 Z=0
    g184: LineSegment StartX=62.0728 StartY=124.221 StartZ=0 EndX=175.022 EndY=124.221 EndZ=0
    g185: LineSegment StartX=179.022 StartY=120.221 StartZ=0 EndX=179.022 EndY=27.0628 EndZ=0
    g186: LineSegment StartX=185.124 StartY=27.0628 StartZ=0 EndX=185.124 EndY=120.221 EndZ=0
    g187: LineSegment StartX=189.124 StartY=124.221 StartZ=0 EndX=302.073 EndY=124.221 EndZ=0
    g188: LineSegment StartX=302.996 StartY=121.665 StartZ=0 EndX=189.124 EndY=27.0628 EndZ=0
    g189: LineSegment StartX=175.022 StartY=27.0628 StartZ=0 EndX=61.1496 EndY=121.665 EndZ=0
    g190: Circle CenterX=61.5791 CenterY=75.4095 CenterZ=0 NormalX=0 NormalY=0 NormalZ=1 AngleXU=0 Radius=1
    g191: Circle CenterX=58.0728 CenterY=77.3346 CenterZ=0 NormalX=0 NormalY=0 NormalZ=1 AngleXU=0 Radius=1
    g192: Circle CenterX=58.0728 CenterY=73.3346 CenterZ=0 NormalX=0 NormalY=0 NormalZ=1 AngleXU=0 Radius=1
    g193: BSplineCurve PolesCount=3 KnotsCount=2 Degree=2 IsPeriodic=0
    g194: GeomPoint X=61.5791 Y=75.4095 Z=0
    g195: GeomPoint X=58.0728 Y=73.3346 Z=0
    g196: Circle CenterX=58.0728 CenterY=-40.8935 CenterZ=0 NormalX=0 NormalY=0 NormalZ=1 AngleXU=0 Radius=1
    g197: Circle CenterX=58.0728 CenterY=-44.8935 CenterZ=0 NormalX=0 NormalY=0 NormalZ=1 AngleXU=0 Radius=1
    g198: Circle CenterX=61.5791 CenterY=-42.9683 CenterZ=0 NormalX=0 NormalY=0 NormalZ=1 AngleXU=0 Radius=1
    g199: BSplineCurve PolesCount=3 KnotsCount=2 Degree=2 IsPeriodic=0
    g200: GeomPoint X=58.0728 Y=-40.8935 Z=0
    g201: GeomPoint X=61.5791 Y=-42.9683 Z=0
    g202: LineSegment StartX=61.5791 StartY=-42.9683 StartZ=0 EndX=165.871 EndY=14.2954 EndZ=0
    g203: LineSegment StartX=165.871 StartY=18.1458 StartZ=0 EndX=61.5791 EndY=75.4095 EndZ=0
    g204: LineSegment StartX=58.0728 StartY=73.3346 StartZ=0 EndX=58.0728 EndY=-40.8935 EndZ=0
    g205: Circle CenterX=302.567 CenterY=-42.9683 CenterZ=0 NormalX=0 NormalY=0 NormalZ=1 AngleXU=0 Radius=1
    g206: Circle CenterX=306.073 CenterY=-44.8935 CenterZ=0 NormalX=0 NormalY=0 NormalZ=1 AngleXU=0 Radius=1
    g207: Circle CenterX=306.073 CenterY=-40.8935 CenterZ=0 NormalX=0 NormalY=0 NormalZ=1 AngleXU=0 Radius=1
    g208: BSplineCurve PolesCount=3 KnotsCount=2 Degree=2 IsPeriodic=0
    g209: GeomPoint X=302.567 Y=-42.9683 Z=0
    g210: GeomPoint X=306.073 Y=-40.8935 Z=0
    g211: Circle CenterX=306.073 CenterY=73.3346 CenterZ=0 NormalX=0 NormalY=0 NormalZ=1 AngleXU=0 Radius=1
    g212: Circle CenterX=306.073 CenterY=77.3346 CenterZ=0 NormalX=0 NormalY=0 NormalZ=1 AngleXU=0 Radius=1
    g213: Circle CenterX=302.567 CenterY=75.4095 CenterZ=0 NormalX=0 NormalY=0 NormalZ=1 AngleXU=0 Radius=1
    g214: BSplineCurve PolesCount=3 KnotsCount=2 Degree=2 IsPeriodic=0
    g215: GeomPoint X=306.073 Y=73.3346 Z=0
    g216: GeomPoint X=302.567 Y=75.4095 Z=0
    g217: LineSegment StartX=302.567 StartY=-42.9683 StartZ=0 EndX=198.275 EndY=14.2954 EndZ=0
    g218: LineSegment StartX=198.275 StartY=18.1458 StartZ=0 EndX=302.567 EndY=75.4095 EndZ=0
    g219: LineSegment StartX=306.073 StartY=73.3346 StartZ=0 EndX=306.073 EndY=-40.8935 EndZ=0
    g220: LineSegment StartX=322.073 StartY=105.865 StartZ=0 EndX=328.643 EndY=105.865 EndZ=0
    g221: LineSegment StartX=318.073 StartY=120.221 StartZ=0 EndX=318.073 EndY=109.865 EndZ=0
    g222: LineSegment StartX=336.157 StartY=107.779 StartZ=0 EndX=362.567 EndY=122.294 EndZ=0
    g223: Circle CenterX=362.073 CenterY=124.221 CenterZ=0 NormalX=0 NormalY=0 NormalZ=1 AngleXU=0 Radius=1
    g224: Circle CenterX=366.073 CenterY=124.221 CenterZ=0 NormalX=0 NormalY=0 NormalZ=1 AngleXU=0 Radius=1
    g225: Circle CenterX=362.567 CenterY=122.294 CenterZ=0 NormalX=0 NormalY=0 NormalZ=1 AngleXU=0 Radius=1
    g226: BSplineCurve PolesCount=3 KnotsCount=2 Degree=2 IsPeriodic=0
    g227: GeomPoint X=362.073 Y=124.221 Z=0
    g228: GeomPoint X=362.567 Y=122.294 Z=0
    g229: Circle CenterX=322.073 CenterY=124.221 CenterZ=0 NormalX=0 NormalY=0 NormalZ=1 AngleXU=0 Radius=1
    g230: Circle CenterX=318.073 CenterY=124.221 CenterZ=0 NormalX=0 NormalY=0 NormalZ=1 AngleXU=0 Radius=1
    g231: Circle CenterX=318.073 CenterY=120.221 CenterZ=0 NormalX=0 NormalY=0 NormalZ=1 AngleXU=0 Radius=1
    g232: BSplineCurve PolesCount=3 KnotsCount=2 Degree=2 IsPeriodic=0
    g233: GeomPoint X=322.073 Y=124.221 Z=0
    g234: GeomPoint X=318.073 Y=120.221 Z=0
    g235: Circle CenterX=322.073 CenterY=105.865 CenterZ=0 NormalX=0 NormalY=0 NormalZ=1 AngleXU=0 Radius=1
    g236: Circle CenterX=318.073 CenterY=105.865 CenterZ=0 NormalX=0 NormalY=0 NormalZ=1 AngleXU=0 Radius=1
    g237: Circle CenterX=318.073 CenterY=109.865 CenterZ=0 NormalX=0 NormalY=0 NormalZ=1 AngleXU=0 Radius=1
    g238: BSplineCurve PolesCount=3 KnotsCount=2 Degree=2 IsPeriodic=0
    g239: GeomPoint X=322.073 Y=105.865 Z=0
    g240: GeomPoint X=318.073 Y=109.865 Z=0
    g241: Circle CenterX=336.157 CenterY=107.779 CenterZ=0 NormalX=0 NormalY=0 NormalZ=1 AngleXU=0 Radius=1
    g242: Circle CenterX=332.651 CenterY=105.853 CenterZ=0 NormalX=0 NormalY=0 NormalZ=1 AngleXU=0 Radius=1
    g243: Circle CenterX=328.643 CenterY=105.865 CenterZ=0 NormalX=0 NormalY=0 NormalZ=1 AngleXU=0 Radius=1
    g244: BSplineCurve PolesCount=3 KnotsCount=2 Degree=2 IsPeriodic=0
    g245: GeomPoint X=336.157 Y=107.779 Z=0
    g246: GeomPoint X=328.643 Y=105.865 Z=0
    g247: LineSegment StartX=322.073 StartY=124.221 StartZ=0 EndX=362.073 EndY=124.221 EndZ=0
    g248: Circle CenterX=371.567 CenterY=-80.8644 CenterZ=0 NormalX=0 NormalY=0 NormalZ=1 AngleXU=0 Radius=1
    g249: Circle CenterX=375.073 CenterY=-82.7896 CenterZ=0 NormalX=0 NormalY=0 NormalZ=1 AngleXU=0 Radius=1
    g250: Circle CenterX=375.073 CenterY=-78.7896 CenterZ=0 NormalX=0 NormalY=0 NormalZ=1 AngleXU=0 Radius=1
    g251: BSplineCurve PolesCount=3 KnotsCount=2 Degree=2 IsPeriodic=0
    g252: GeomPoint X=371.567 Y=-80.8644 Z=0
    g253: GeomPoint X=375.073 Y=-78.7896 Z=0
    g254: Circle CenterX=321.579 CenterY=-53.4075 CenterZ=0 NormalX=0 NormalY=0 NormalZ=1 AngleXU=0 Radius=1
    g255: Circle CenterX=318.073 CenterY=-51.4823 CenterZ=0 NormalX=0 NormalY=0 NormalZ=1 AngleXU=0 Radius=1
    g256: Circle CenterX=318.073 CenterY=-47.4805 CenterZ=0 NormalX=0 NormalY=0 NormalZ=1 AngleXU=0 Radius=1
    g257: BSplineCurve PolesCount=3 KnotsCount=2 Degree=2 IsPeriodic=0
    g258: GeomPoint X=321.579 Y=-53.4075 Z=0
    g259: GeomPoint X=318.073 Y=-47.4805 Z=0
    g260: LineSegment StartX=371.567 StartY=-80.8644 StartZ=0 EndX=321.579 EndY=-53.4075 EndZ=0
    g261: Circle CenterX=321.579 CenterY=-67.3492 CenterZ=0 NormalX=0 NormalY=0 NormalZ=1 AngleXU=0 Radius=1
    g262: Circle CenterX=318.073 CenterY=-65.424 CenterZ=0 NormalX=0 NormalY=0 NormalZ=1 AngleXU=0 Radius=1
    g263: Circle CenterX=318.073 CenterY=-69.424 CenterZ=0 NormalX=0 NormalY=0 NormalZ=1 AngleXU=0 Radius=1
    g264: BSplineCurve PolesCount=3 KnotsCount=2 Degree=2 IsPeriodic=0
    g265: GeomPoint X=321.579 Y=-67.3492 Z=0
    g266: GeomPoint X=318.073 Y=-69.424 Z=0
    g267: Circle CenterX=362.567 CenterY=-89.8542 CenterZ=0 NormalX=0 NormalY=0 NormalZ=1 AngleXU=0 Radius=1
    g268: Circle CenterX=366.073 CenterY=-91.7794 CenterZ=0 NormalX=0 NormalY=0 NormalZ=1 AngleXU=0 Radius=1
    g269: Circle CenterX=362.073 CenterY=-91.7794 CenterZ=0 NormalX=0 NormalY=0 NormalZ=1 AngleXU=0 Radius=1
    g270: BSplineCurve PolesCount=3 KnotsCount=2 Degree=2 IsPeriodic=0
    g271: GeomPoint X=362.567 Y=-89.8542 Z=0
    g272: GeomPoint X=362.073 Y=-91.7794 Z=0
    g273: Circle CenterX=322.073 CenterY=-91.7794 CenterZ=0 NormalX=0 NormalY=0 NormalZ=1 AngleXU=0 Radius=1
    g274: Circle CenterX=318.073 CenterY=-91.7794 CenterZ=0 NormalX=0 NormalY=0 NormalZ=1 AngleXU=0 Radius=1
    g275: Circle CenterX=318.073 CenterY=-87.7794 CenterZ=0 NormalX=0 NormalY=0 NormalZ=1 AngleXU=0 Radius=1
    g276: BSplineCurve PolesCount=3 KnotsCount=2 Degree=2 IsPeriodic=0
    g277: GeomPoint X=322.073 Y=-91.7794 Z=0
    g278: GeomPoint X=318.073 Y=-87.7794 Z=0
    g279: LineSegment StartX=362.567 StartY=-89.8542 StartZ=0 EndX=321.579 EndY=-67.3492 EndZ=0
    g280: LineSegment StartX=318.073 StartY=-69.424 StartZ=0 EndX=318.073 EndY=-87.7794 EndZ=0
    g281: LineSegment StartX=322.073 StartY=-91.7794 StartZ=0 EndX=362.073 EndY=-91.7794 EndZ=0
    g282: Circle CenterX=2.07281 CenterY=124.221 CenterZ=0 NormalX=0 NormalY=0 NormalZ=1 AngleXU=0 Radius=1
    g283: Circle CenterX=1.57905 CenterY=122.295 CenterZ=0 NormalX=0 NormalY=0 NormalZ=1 AngleXU=0 Radius=1
    g284: BSplineCurve PolesCount=3 KnotsCount=2 Degree=2 IsPeriodic=0
    g285: GeomPoint X=2.07281 Y=124.221 Z=0
    g286: GeomPoint X=1.57905 Y=122.295 Z=0
    g287: Circle CenterX=42.0728 CenterY=124.221 CenterZ=0 NormalX=0 NormalY=0 NormalZ=1 AngleXU=0 Radius=1
    g288: Circle CenterX=46.0728 CenterY=124.221 CenterZ=0 NormalX=0 NormalY=0 NormalZ=1 AngleXU=0 Radius=1
    g289: Circle CenterX=46.0728 CenterY=120.221 CenterZ=0 NormalX=0 NormalY=0 NormalZ=1 AngleXU=0 Radius=1
    g290: BSplineCurve PolesCount=3 KnotsCount=2 Degree=2 IsPeriodic=0
    g291: GeomPoint X=42.0728 Y=124.221 Z=0
    g292: GeomPoint X=46.0728 Y=120.221 Z=0
    g293: Circle CenterX=46.0728 CenterY=109.865 CenterZ=0 NormalX=0 NormalY=0 NormalZ=1 AngleXU=0 Radius=1
    g294: Circle CenterX=46.0728 CenterY=105.865 CenterZ=0 NormalX=0 NormalY=0 NormalZ=1 AngleXU=0 Radius=1
    g295: Circle CenterX=42.0728 CenterY=105.865 CenterZ=0 NormalX=0 NormalY=0 NormalZ=1 AngleXU=0 Radius=1
    g296: BSplineCurve PolesCount=3 KnotsCount=2 Degree=2 IsPeriodic=0
    g297: GeomPoint X=46.0728 Y=109.865 Z=0
    g298: GeomPoint X=42.0728 Y=105.865 Z=0
    g299: Circle CenterX=35.5028 CenterY=105.865 CenterZ=0 NormalX=0 NormalY=0 NormalZ=1 AngleXU=0 Radius=1
    g300: Circle CenterX=31.5028 CenterY=105.865 CenterZ=0 NormalX=0 NormalY=0 NormalZ=1 AngleXU=0 Radius=1
    g301: Circle CenterX=27.9965 CenterY=107.79 CenterZ=0 NormalX=0 NormalY=0 NormalZ=1 AngleXU=0 Radius=1
    g302: BSplineCurve PolesCount=3 KnotsCount=2 Degree=2 IsPeriodic=0
    g303: GeomPoint X=35.5028 Y=105.865 Z=0
    g304: GeomPoint X=27.9965 Y=107.79 Z=0
    g305: LineSegment StartX=2.07281 StartY=124.221 StartZ=0 EndX=42.0728 EndY=124.221 EndZ=0
    g306: LineSegment StartX=46.0728 StartY=120.221 StartZ=0 EndX=46.0728 EndY=109.865 EndZ=0
    g307: LineSegment StartX=42.0728 StartY=105.865 StartZ=0 EndX=35.5028 EndY=105.865 EndZ=0
    g308: LineSegment StartX=27.9965 StartY=107.79 StartZ=0 EndX=1.57905 EndY=122.295 EndZ=0
    g309: Circle CenterX=42.5666 CenterY=-67.3492 CenterZ=0 NormalX=0 NormalY=0 NormalZ=1 AngleXU=0 Radius=1
    g310: Circle CenterX=46.0728 CenterY=-65.424 CenterZ=0 NormalX=0 NormalY=0 NormalZ=1 AngleXU=0 Radius=1
    g311: Circle CenterX=46.0728 CenterY=-69.424 CenterZ=0 NormalX=0 NormalY=0 NormalZ=1 AngleXU=0 Radius=1
    g312: BSplineCurve PolesCount=3 KnotsCount=2 Degree=2 IsPeriodic=0
    g313: GeomPoint X=42.5666 Y=-67.3492 Z=0
    g314: GeomPoint X=46.0728 Y=-69.424 Z=0
    g315: Circle CenterX=46.0728 CenterY=-87.7794 CenterZ=0 NormalX=0 NormalY=0 NormalZ=1 AngleXU=0 Radius=1
    g316: Circle CenterX=46.0728 CenterY=-91.7794 CenterZ=0 NormalX=0 NormalY=0 NormalZ=1 AngleXU=0 Radius=1
    g317: Circle CenterX=42.0728 CenterY=-91.7794 CenterZ=0 NormalX=0 NormalY=0 NormalZ=1 AngleXU=0 Radius=1
    g318: BSplineCurve PolesCount=3 KnotsCount=2 Degree=2 IsPeriodic=0
    g319: GeomPoint X=46.0728 Y=-87.7794 Z=0
    g320: GeomPoint X=42.0728 Y=-91.7794 Z=0
    g321: Circle CenterX=2.07281 CenterY=-91.7794 CenterZ=0 NormalX=0 NormalY=0 NormalZ=1 AngleXU=0 Radius=1
    g322: Circle CenterX=-1.92719 CenterY=-91.7794 CenterZ=0 NormalX=0 NormalY=0 NormalZ=1 AngleXU=0 Radius=1
    g323: Circle CenterX=1.57905 CenterY=-89.8542 CenterZ=0 NormalX=0 NormalY=0 NormalZ=1 AngleXU=0 Radius=1
    g324: BSplineCurve PolesCount=3 KnotsCount=2 Degree=2 IsPeriodic=0
    g325: GeomPoint X=2.07281 Y=-91.7794 Z=0
    g326: GeomPoint X=1.57905 Y=-89.8542 Z=0
    g327: LineSegment StartX=2.07281 StartY=-91.7794 StartZ=0 EndX=42.0728 EndY=-91.7794 EndZ=0
    g328: LineSegment StartX=46.0728 StartY=-87.7794 StartZ=0 EndX=46.0728 EndY=-69.424 EndZ=0
    g329: LineSegment StartX=42.5666 StartY=-67.3492 StartZ=0 EndX=1.57905 EndY=-89.8542 EndZ=0
    g330: Circle CenterX=322.073 CenterY=76.4095 CenterZ=0 NormalX=0 NormalY=0 NormalZ=1 AngleXU=0 Radius=4
    g331: BSplineCurve PolesCount=3 KnotsCount=2 Degree=2 IsPeriodic=0
    g332: GeomPoint X=318.073 Y=72.4095 Z=0
    g333: GeomPoint X=322.073 Y=76.4095 Z=0
    g334: Circle CenterX=375.073 CenterY=72.4095 CenterZ=0 NormalX=0 NormalY=0 NormalZ=1 AngleXU=0 Radius=1
    g335: Circle CenterX=375.073 CenterY=76.4095 CenterZ=0 NormalX=0 NormalY=0 NormalZ=1 AngleXU=0 Radius=1
    g336: Circle CenterX=371.073 CenterY=76.4095 CenterZ=0 NormalX=0 NormalY=0 NormalZ=1 AngleXU=0 Radius=1
    g337: BSplineCurve PolesCount=3 KnotsCount=2 Degree=2 IsPeriodic=0
    g338: GeomPoint X=375.073 Y=72.4095 Z=0
    g339: GeomPoint X=371.073 Y=76.4095 Z=0
    g340: LineSegment StartX=322.073 StartY=76.4095 StartZ=0 EndX=371.073 EndY=76.4095 EndZ=0
    g341: LineSegment StartX=318.073 StartY=72.4095 StartZ=0 EndX=318.073 EndY=-47.4805 EndZ=0
    g342: LineSegment StartX=375.073 StartY=72.4095 StartZ=0 EndX=375.073 EndY=-78.7896 EndZ=0
    g343: ArcOfCircle CenterX=-26.9272 CenterY=22.1087 CenterZ=0 NormalX=0 NormalY=0 NormalZ=1 AngleXU=0 Radius=4 StartAngle=5e-16 EndAngle=3.14159
    g344: LineSegment StartX=-22.9272 StartY=22.1087 StartZ=0 EndX=-18.9272 EndY=-83.7794 EndZ=0
    g345: LineSegment StartX=-34.9272 StartY=-83.7794 StartZ=0 EndX=-30.9272 EndY=22.1087 EndZ=0
    g346: ArcOfCircle CenterX=391.073 CenterY=22.1087 CenterZ=0 NormalX=0 NormalY=0 NormalZ=1 AngleXU=0 Radius=4 StartAngle=0 EndAngle=3.14159
    g347: LineSegment StartX=387.073 StartY=22.1087 StartZ=0 EndX=383.073 EndY=-83.7794 EndZ=0
    g348: LineSegment StartX=395.073 StartY=22.1087 StartZ=0 EndX=399.073 EndY=-83.7794 EndZ=0
    g349: LineSegment StartX=-10.8137 StartY=77.6538 StartZ=0 EndX=-6.81372 EndY=77.6538 EndZ=0
    g350: LineSegment StartX=-12.1541 StartY=75.7859 StartZ=0 EndX=-12.1541 EndY=71.7859 EndZ=0
    g351: LineSegment StartX=45.0299 StartY=77.4064 StartZ=0 EndX=41.0299 EndY=77.4064 EndZ=0
    g352: LineSegment StartX=47.2847 StartY=75.644 StartZ=0 EndX=47.2847 EndY=71.644 EndZ=0
    g353: LineSegment StartX=47.0795 StartY=-50.9775 StartZ=0 EndX=47.0795 EndY=-46.9775 EndZ=0
    g354: LineSegment StartX=45.6694 StartY=-52.7433 StartZ=0 EndX=42.1632 EndY=-54.6684 EndZ=0
    g355: LineSegment StartX=-8.4454 StartY=-83.4031 StartZ=0 EndX=-4.93917 EndY=-81.4779 EndZ=0
    g356: LineSegment StartX=-11.8576 StartY=-81.9627 StartZ=0 EndX=-11.8576 EndY=-77.9627 EndZ=0
  constraints (589):
    c: Coincident(g0,g2)
    c: Block(g0)
    c: Block(g1)
    c: Vertical(g3)
    c: Vertical(g4)
    c: Block(g4)
    c: Block(g3)
    c: Weight(g7) = 1
    c: Equal(g7,g8)
    c: Equal(g7,g9)
    c: InternalAlignment(g7,g10)
    c: InternalAlignment(g8,g10)
    c: InternalAlignment(g9,g10)
    c: InternalAlignment(g11,g10)
    c: InternalAlignment(g12,g10)
    c: Weight(g13) = 1
    c: Equal(g13,g14)
    c: Equal(g13,g15)
    c: InternalAlignment(g13,g16)
    c: InternalAlignment(g14,g16)
    c: InternalAlignment(g15,g16)
    c: InternalAlignment(g17,g16)
    c: InternalAlignment(g18,g16)
    c: Block(g16)
    c: Block(g10)
    c: Weight(g19) = 1
    c: Equal(g19,g20)
    c: Equal(g19,g21)
    c: InternalAlignment(g19,g22)
    c: InternalAlignment(g20,g22)
    c: InternalAlignment(g21,g22)
    c: InternalAlignment(g23,g22)
    c: InternalAlignment(g24,g22)
    c: Weight(g25) = 1
    c: Equal(g25,g26)
    c: Equal(g25,g27)
    c: InternalAlignment(g25,g28)
    c: InternalAlignment(g26,g28)
    c: InternalAlignment(g27,g28)
    c: InternalAlignment(g29,g28)
    c: InternalAlignment(g30,g28)
    c: Block(g28)
    c: Block(g22)
    c: Weight(g31) = 1
    c: Equal(g31,g32)
    c: Equal(g31,g33)
    c: InternalAlignment(g31,g34)
    c: InternalAlignment(g32,g34)
    c: InternalAlignment(g33,g34)
    c: InternalAlignment(g35,g34)
    c: InternalAlignment(g36,g34)
    c: Weight(g37) = 1
    c: Equal(g37,g38)
    c: Equal(g37,g39)
    c: InternalAlignment(g37,g40)
    c: InternalAlignment(g38,g40)
    c: InternalAlignment(g39,g40)
    c: InternalAlignment(g41,g40)
    c: InternalAlignment(g42,g40)
    c: Block(g34)
    c: Block(g40)
    c: Coincident(g43,g4)
    c: Coincident(g43,g3)
    c: Horizontal(g43)
    c: Distance(g43) = 450
    c: Coincident(g44,g4)
    c: Coincident(g44,g3)
    c: Horizontal(g44)
    c: Horizontal(g45)
    c: Coincident(g2,g45)
    c: Block(g45)
    c: Coincident(g1,g45)
    c: Weight(g46) = 1
    c: Equal(g46,g47)
    c: Equal(g46,g48)
    c: InternalAlignment(g46,g49)
    c: InternalAlignment(g47,g49)
    c: InternalAlignment(g48,g49)
    c: InternalAlignment(g50,g49)
    c: InternalAlignment(g51,g49)
    c: Block(g49)
    c: Weight(g52) = 1
    c: Equal(g52,g53)
    c: Equal(g52,g54)
    c: InternalAlignment(g52,g55)
    c: InternalAlignment(g53,g55)
    c: InternalAlignment(g54,g55)
    c: InternalAlignment(g56,g55)
    c: InternalAlignment(g57,g55)
    c: Block(g55)
    c: Weight(g58) = 1
    c: Equal(g58,g59)
    c: Equal(g58,g60)
    c: InternalAlignment(g58,g61)
    c: InternalAlignment(g59,g61)
    c: InternalAlignment(g60,g61)
    c: InternalAlignment(g62,g61)
    c: InternalAlignment(g63,g61)
    c: Block(g61)
    c: Weight(g64) = 1
    c: Equal(g64,g65)
    c: Equal(g64,g66)
    c: InternalAlignment(g64,g67)
    c: InternalAlignment(g65,g67)
    c: InternalAlignment(g66,g67)
    c: InternalAlignment(g68,g67)
    c: InternalAlignment(g69,g67)
    c: Block(g67)
    c: Weight(g70) = 1
    c: Equal(g70,g71)
    c: Equal(g70,g72)
    c: InternalAlignment(g70,g73)
    c: InternalAlignment(g71,g73)
    c: InternalAlignment(g72,g73)
    c: InternalAlignment(g74,g73)
    c: InternalAlignment(g75,g73)
    c: Weight(g76) = 1
    c: Equal(g76,g77)
    c: Equal(g76,g78)
    c: InternalAlignment(g76,g79)
    c: InternalAlignment(g77,g79)
    c: InternalAlignment(g78,g79)
    c: InternalAlignment(g80,g79)
    c: InternalAlignment(g81,g79)
    c: Block(g73)
    c: Block(g79)
    c: Coincident(g82,g73)
    c: Coincident(g82,g79)
    c: Vertical(g82)
    c: Coincident(g83,g73)
    c: Coincident(g83,g55)
    c: Coincident(g84,g55)
    c: Coincident(g84,g79)
    c: Weight(g85) = 1
    c: Equal(g85,g86)
    c: Equal(g85,g87)
    c: InternalAlignment(g85,g88)
    c: InternalAlignment(g86,g88)
    c: InternalAlignment(g87,g88)
    c: InternalAlignment(g89,g88)
    c: InternalAlignment(g90,g88)
    c: Weight(g91) = 1
    c: Equal(g91,g92)
    c: Equal(g91,g93)
    c: InternalAlignment(g91,g94)
    c: InternalAlignment(g92,g94)
    c: InternalAlignment(g93,g94)
    c: InternalAlignment(g95,g94)
    c: InternalAlignment(g96,g94)
    c: Block(g88)
    c: Block(g94)
    c: Coincident(g97,g88)
    c: Coincident(g97,g94)
    c: Vertical(g97)
    c: Coincident(g98,g88)
    c: Coincident(g98,g49)
    c: Coincident(g99,g49)
    c: Coincident(g99,g94)
    c: Weight(g100) = 1
    c: Equal(g100,g101)
    c: Equal(g100,g102)
    c: InternalAlignment(g100,g103)
    c: InternalAlignment(g101,g103)
    c: InternalAlignment(g102,g103)
    c: InternalAlignment(g104,g103)
    c: InternalAlignment(g105,g103)
    c: Weight(g106) = 1
    c: Equal(g106,g107)
    c: Equal(g106,g108)
    c: InternalAlignment(g106,g109)
    c: InternalAlignment(g107,g109)
    c: InternalAlignment(g108,g109)
    c: InternalAlignment(g110,g109)
    c: InternalAlignment(g111,g109)
    c: Block(g103)
    c: Block(g109)
    c: Coincident(g112,g103)
    c: Coincident(g112,g109)
    c: Vertical(g112)
    c: Coincident(g113,g109)
    c: Coincident(g113,g67)
    c: Coincident(g114,g67)
    c: Coincident(g114,g103)
    c: Weight(g115) = 1
    c: Equal(g115,g116)
    c: Equal(g115,g117)
    c: InternalAlignment(g115,g118)
    c: InternalAlignment(g116,g118)
    c: InternalAlignment(g117,g118)
    c: InternalAlignment(g119,g118)
    c: InternalAlignment(g120,g118)
    c: Weight(g121) = 1
    c: Equal(g121,g122)
    c: Equal(g121,g123)
    c: InternalAlignment(g121,g124)
    c: InternalAlignment(g122,g124)
    c: InternalAlignment(g123,g124)
    c: InternalAlignment(g125,g124)
    c: InternalAlignment(g126,g124)
    c: Block(g118)
    c: Block(g124)
    c: Coincident(g127,g118)
    c: Coincident(g127,g124)
    c: Vertical(g127)
    c: Coincident(g128,g124)
    c: Coincident(g128,g61)
    c: Coincident(g129,g61)
    c: Coincident(g129,g118)
    c: Weight(g130) = 1
    c: Equal(g130,g131)
    c: Equal(g130,g132)
    c: InternalAlignment(g130,g133)
    c: InternalAlignment(g131,g133)
    c: InternalAlignment(g132,g133)
    c: InternalAlignment(g134,g133)
    c: InternalAlignment(g135,g133)
    c: Weight(g136) = 1
    c: Equal(g136,g137)
    c: Equal(g136,g138)
    c: InternalAlignment(g136,g139)
    c: InternalAlignment(g137,g139)
    c: InternalAlignment(g138,g139)
    c: InternalAlignment(g140,g139)
    c: InternalAlignment(g141,g139)
    c: Weight(g142) = 1
    c: Equal(g142,g143)
    c: Equal(g142,g144)
    c: InternalAlignment(g142,g145)
    c: InternalAlignment(g143,g145)
    c: InternalAlignment(g144,g145)
    c: InternalAlignment(g146,g145)
    c: InternalAlignment(g147,g145)
    c: Weight(g148) = 1
    c: Equal(g148,g149)
    c: Equal(g148,g150)
    c: InternalAlignment(g148,g151)
    c: InternalAlignment(g149,g151)
    c: InternalAlignment(g150,g151)
    c: InternalAlignment(g152,g151)
    c: InternalAlignment(g153,g151)
    c: Block(g151)
    c: Block(g145)
    c: Block(g139)
    c: Block(g133)
    c: Coincident(g154,g28)
    c: Coincident(g154,g151)
    c: Coincident(g155,g151)
    c: Coincident(g155,g145)
    c: Horizontal(g155)
    c: Coincident(g156,g145)
    c: Coincident(g156,g28)
    c: Vertical(g156)
    c: Coincident(g157,g22)
    c: Coincident(g157,g139)
    c: Vertical(g157)
    c: Coincident(g158,g139)
    c: Coincident(g158,g133)
    c: Horizontal(g158)
    c: Coincident(g159,g133)
    c: Coincident(g159,g22)
    c: Weight(g160) = 1
    c: Equal(g160,g161)
    c: Equal(g160,g162)
    c: InternalAlignment(g160,g163)
    c: InternalAlignment(g161,g163)
    c: InternalAlignment(g162,g163)
    c: InternalAlignment(g164,g163)
    c: InternalAlignment(g165,g163)
    c: Weight(g166) = 1
    c: Equal(g166,g167)
    c: Equal(g166,g168)
    c: InternalAlignment(g166,g169)
    c: InternalAlignment(g167,g169)
    c: InternalAlignment(g168,g169)
    c: InternalAlignment(g170,g169)
    c: InternalAlignment(g171,g169)
    c: Weight(g172) = 1
    c: Equal(g172,g173)
    c: Equal(g172,g174)
    c: InternalAlignment(g172,g175)
    c: InternalAlignment(g173,g175)
    c: InternalAlignment(g174,g175)
    c: InternalAlignment(g176,g175)
    c: InternalAlignment(g177,g175)
    c: Weight(g178) = 1
    c: Equal(g178,g179)
    c: Equal(g178,g180)
    c: InternalAlignment(g178,g181)
    c: InternalAlignment(g179,g181)
    c: InternalAlignment(g180,g181)
    c: InternalAlignment(g182,g181)
    c: InternalAlignment(g183,g181)
    c: Block(g181)
    c: Block(g175)
    c: Block(g169)
    c: Block(g163)
    c: Coincident(g184,g181)
    c: Coincident(g184,g175)
    c: Horizontal(g184)
    c: Coincident(g185,g175)
    c: Coincident(g185,g10)
    c: Vertical(g185)
    c: Coincident(g186,g16)
    c: Coincident(g186,g169)
    c: Vertical(g186)
    c: Coincident(g187,g169)
    c: Coincident(g187,g163)
    c: Horizontal(g187)
    c: Coincident(g188,g163)
    c: Coincident(g188,g16)
    c: Coincident(g189,g10)
    c: Weight(g190) = 1
    c: Equal(g190,g191)
    c: Equal(g190,g192)
    c: InternalAlignment(g190,g193)
    c: InternalAlignment(g191,g193)
    c: InternalAlignment(g192,g193)
    c: InternalAlignment(g194,g193)
    c: InternalAlignment(g195,g193)
    c: Weight(g196) = 1
    c: Equal(g196,g197)
    c: Equal(g196,g198)
    c: InternalAlignment(g196,g199)
    c: InternalAlignment(g197,g199)
    c: InternalAlignment(g198,g199)
    c: InternalAlignment(g200,g199)
    c: InternalAlignment(g201,g199)
    c: Block(g199)
    c: Block(g193)
    c: Coincident(g202,g199)
    c: Coincident(g202,g34)
    c: Coincident(g203,g34)
    c: Coincident(g203,g193)
    c: Coincident(g204,g193)
    c: Coincident(g204,g199)
    c: Vertical(g204)
    c: Weight(g205) = 1
    c: Equal(g205,g206)
    c: Equal(g205,g207)
    c: InternalAlignment(g205,g208)
    c: InternalAlignment(g206,g208)
    c: InternalAlignment(g207,g208)
    c: InternalAlignment(g209,g208)
    c: InternalAlignment(g210,g208)
    c: Weight(g211) = 1
    c: Equal(g211,g212)
    c: Equal(g211,g213)
    c: InternalAlignment(g211,g214)
    c: InternalAlignment(g212,g214)
    c: InternalAlignment(g213,g214)
    c: InternalAlignment(g215,g214)
    c: InternalAlignment(g216,g214)
    c: Block(g214)
    c: Block(g208)
    c: Coincident(g217,g208)
    c: Coincident(g217,g40)
    c: Coincident(g218,g40)
    c: Coincident(g218,g214)
    c: Coincident(g219,g214)
    c: Coincident(g219,g208)
    c: Vertical(g219)
    c: Horizontal(g220)
    c: Block(g220)
    c: Vertical(g221)
    c: Block(g221)
    c: Block(g222)
    c: Weight(g223) = 1
    c: Equal(g223,g224)
    c: Equal(g223,g225)
    c: InternalAlignment(g223,g226)
    c: InternalAlignment(g224,g226)
    c: InternalAlignment(g225,g226)
    c: InternalAlignment(g227,g226)
    c: InternalAlignment(g228,g226)
    c: Weight(g229) = 1
    c: Equal(g229,g230)
    c: Equal(g229,g231)
    c: InternalAlignment(g229,g232)
    c: InternalAlignment(g230,g232)
    c: InternalAlignment(g231,g232)
    c: InternalAlignment(g233,g232)
    c: InternalAlignment(g234,g232)
    c: Weight(g235) = 1
    c: Equal(g235,g236)
    c: Equal(g235,g237)
    c: InternalAlignment(g235,g238)
    c: InternalAlignment(g236,g238)
    c: InternalAlignment(g237,g238)
    c: InternalAlignment(g239,g238)
    c: InternalAlignment(g240,g238)
    c: Weight(g241) = 1
    c: Equal(g241,g242)
    c: Equal(g241,g243)
    c: InternalAlignment(g241,g244)
    c: InternalAlignment(g242,g244)
    c: InternalAlignment(g243,g244)
    c: InternalAlignment(g245,g244)
    c: InternalAlignment(g246,g244)
    c: Block(g226)
    c: Block(g232)
    c: Block(g238)
    c: Block(g244)
    c: Coincident(g247,g232)
    c: Coincident(g247,g226)
    c: Horizontal(g247)
    c: Block(g189)
    c: Weight(g248) = 1
    c: Equal(g248,g249)
    c: Equal(g248,g250)
    c: InternalAlignment(g248,g251)
    c: InternalAlignment(g249,g251)
    c: InternalAlignment(g250,g251)
    c: InternalAlignment(g252,g251)
    c: InternalAlignment(g253,g251)
    c: Weight(g254) = 1
    c: Equal(g254,g255)
    c: Equal(g254,g256)
    c: InternalAlignment(g254,g257)
    c: InternalAlignment(g255,g257)
    c: InternalAlignment(g256,g257)
    c: InternalAlignment(g258,g257)
    c: InternalAlignment(g259,g257)
    c: Block(g251)
    c: Block(g257)
    c: Coincident(g260,g251)
    c: Coincident(g260,g257)
    c: Weight(g261) = 1
    c: Equal(g261,g262)
    c: Equal(g261,g263)
    c: InternalAlignment(g261,g264)
    c: InternalAlignment(g262,g264)
    c: InternalAlignment(g263,g264)
    c: InternalAlignment(g265,g264)
    c: InternalAlignment(g266,g264)
    c: Weight(g267) = 1
    c: Equal(g267,g268)
    c: Equal(g267,g269)
    c: InternalAlignment(g267,g270)
    c: InternalAlignment(g268,g270)
    c: InternalAlignment(g269,g270)
    c: InternalAlignment(g271,g270)
    c: InternalAlignment(g272,g270)
    c: Weight(g273) = 1
    c: Equal(g273,g274)
    c: Equal(g273,g275)
    c: InternalAlignment(g273,g276)
    c: InternalAlignment(g274,g276)
    c: InternalAlignment(g275,g276)
    c: InternalAlignment(g277,g276)
    c: InternalAlignment(g278,g276)
    c: Block(g276)
    c: Block(g270)
    c: Block(g264)
    c: Coincident(g279,g270)
    c: Coincident(g279,g264)
    c: Coincident(g280,g264)
    c: Coincident(g280,g276)
    c: Vertical(g280)
    c: Coincident(g281,g276)
    c: Coincident(g281,g270)
    c: Horizontal(g281)
    c: Weight(g282) = 1
    c: Equal(g282,g283)
    c: InternalAlignment(g282,g284)
    c: InternalAlignment(g283,g284)
    c: InternalAlignment(g285,g284)
    c: InternalAlignment(g286,g284)
    c: Weight(g287) = 1
    c: InternalAlignment(g288,g290)
    c: InternalAlignment(g289,g290)
    c: InternalAlignment(g291,g290)
    c: InternalAlignment(g292,g290)
    c: Weight(g293) = 1
    c: Equal(g293,g294)
    c: Equal(g293,g295)
    c: InternalAlignment(g293,g296)
    c: InternalAlignment(g294,g296)
    c: InternalAlignment(g295,g296)
    c: InternalAlignment(g297,g296)
    c: InternalAlignment(g298,g296)
    c: Equal(g299,g300)
    c: Equal(g299,g301)
    c: InternalAlignment(g299,g302)
    c: InternalAlignment(g300,g302)
    c: InternalAlignment(g301,g302)
    c: InternalAlignment(g303,g302)
    c: InternalAlignment(g304,g302)
    c: Block(g290)
    c: Block(g296)
    c: Block(g302)
    c: Block(g284)
    c: Coincident(g305,g284)
    c: Coincident(g305,g290)
    c: Horizontal(g305)
    c: Coincident(g306,g290)
    c: Coincident(g306,g296)
    c: Vertical(g306)
    c: Coincident(g307,g296)
    c: Coincident(g307,g302)
    c: Horizontal(g307)
    c: Coincident(g308,g302)
    c: Coincident(g308,g284)
    c: Weight(g309) = 1
    c: Equal(g309,g310)
    c: Equal(g309,g311)
    c: InternalAlignment(g309,g312)
    c: InternalAlignment(g310,g312)
    c: InternalAlignment(g311,g312)
    c: InternalAlignment(g313,g312)
    c: InternalAlignment(g314,g312)
    c: Weight(g315) = 1
    c: Equal(g315,g316)
    c: Equal(g315,g317)
    c: InternalAlignment(g315,g318)
    c: InternalAlignment(g316,g318)
    c: InternalAlignment(g317,g318)
    c: InternalAlignment(g319,g318)
    c: InternalAlignment(g320,g318)
    c: Weight(g321) = 1
    c: Equal(g321,g322)
    c: Equal(g321,g323)
    c: InternalAlignment(g321,g324)
    c: InternalAlignment(g322,g324)
    c: InternalAlignment(g323,g324)
    c: InternalAlignment(g325,g324)
    c: InternalAlignment(g326,g324)
    c: Block(g324)
    c: Block(g318)
    c: Block(g312)
    c: Coincident(g327,g324)
    c: Coincident(g327,g318)
    c: Horizontal(g327)
    c: Coincident(g328,g318)
    c: Coincident(g328,g312)
    c: Vertical(g328)
    c: Coincident(g329,g312)
    c: Coincident(g329,g324)
    c: InternalAlignment(g330,g331)
    c: InternalAlignment(g332,g331)
    c: InternalAlignment(g333,g331)
    c: Block(g331)
    c: Equal(g334,g335)
    c: Equal(g334,g336)
    c: InternalAlignment(g334,g337)
    c: InternalAlignment(g335,g337)
    c: InternalAlignment(g336,g337)
    c: InternalAlignment(g338,g337)
    c: InternalAlignment(g339,g337)
    c: Block(g337)
    c: Coincident(g340,g331)
    c: Horizontal(g340)
    c: Block(g340)
    c: Coincident(g341,g331)
    c: Coincident(g341,g257)
    c: Vertical(g341)
    c: Coincident(g342,g337)
    c: Coincident(g342,g251)
    c: Vertical(g342)
    c: Block(g343)
    c: Block(g5)
    c: Distance(g341) = 119.89
    c: Coincident(g344,g343)
    c: Coincident(g344,g5)
    c: Coincident(g345,g5)
    c: Coincident(g345,g343)
    c: Block(g6)
    c: Block(g346)
    c: Coincident(g347,g346)
    c: Coincident(g347,g6)
    c: Coincident(g348,g346)
    c: Coincident(g348,g6)
    c: Block(g348)
    c: Block(g347)
    c: Horizontal(g349)
    c: Vertical(g350)
    c: Horizontal(g351)
    c: Vertical(g352)
    c: Vertical(g353)
    c: Vertical(g356)
    c: Parallel(g0,g355)
    c: Parallel(g354,g0)
    c: Distance(g354) = 4
    c: Distance(g353) = 4
    c: Distance(g355) = 4
    c: Distance(g356) = 4
    c: Distance(g349) = 4
    c: Distance(g350) = 4
    c: Distance(g351) = 4
    c: Distance(g352) = 4
